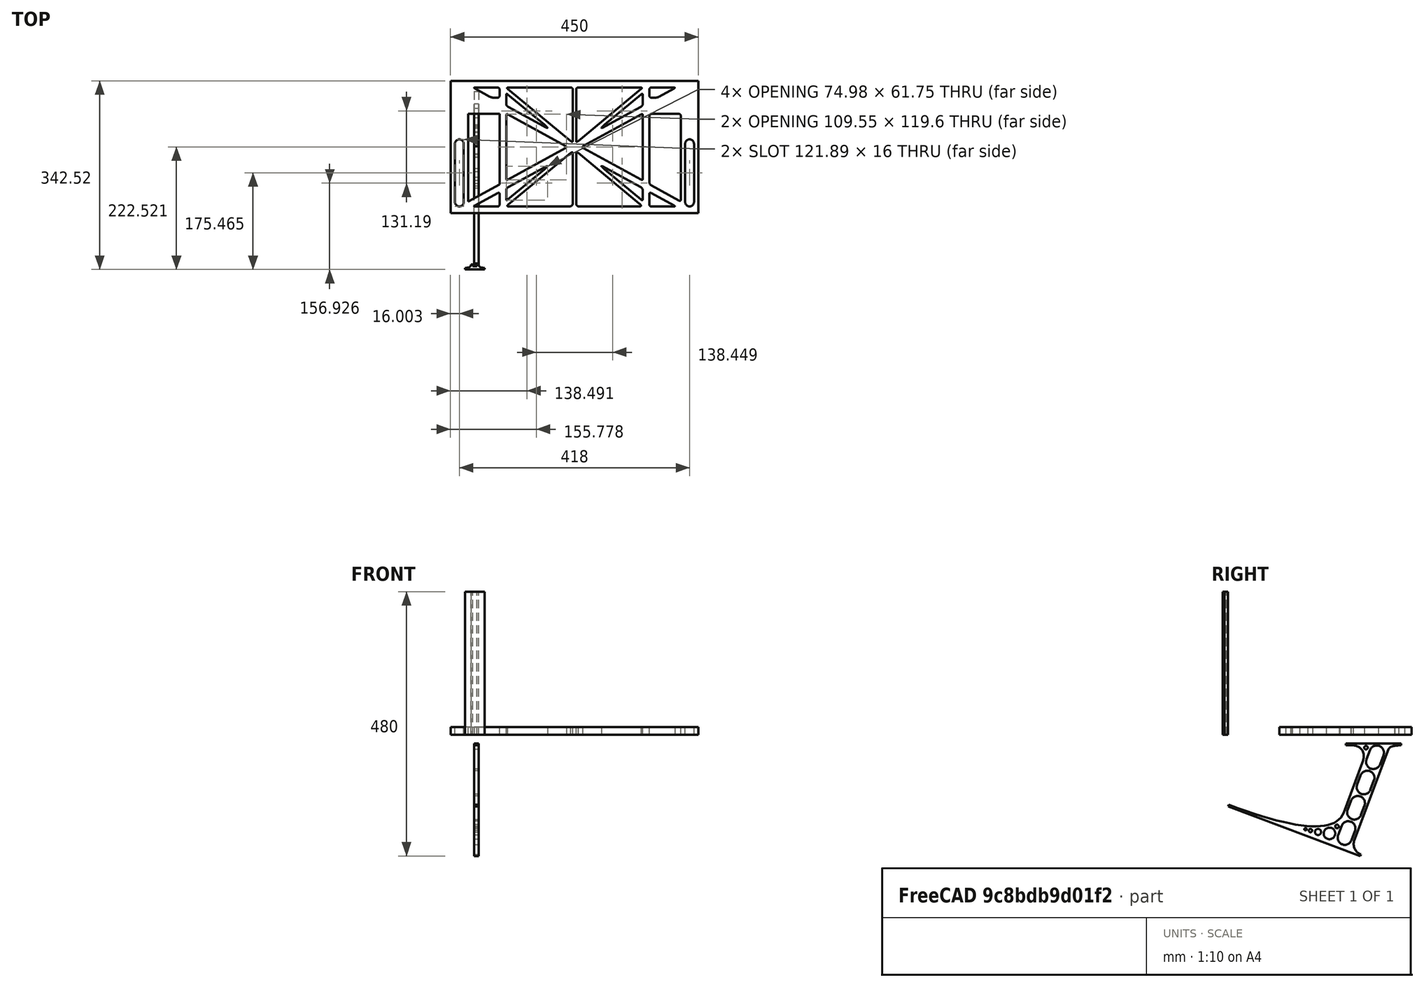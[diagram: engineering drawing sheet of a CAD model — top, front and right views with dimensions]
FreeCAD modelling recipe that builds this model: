
FCSTD DOCUMENT  (FreeCAD 0.19R0.19.2)
Label: laptopStand141FCStd
License: All rights reserved
LicenseURL: http://en.wikipedia.org/wiki/All_rights_reserved
objects: Sketcher::SketchObject×4, Part::Extrusion×3
note: 7 computed .brp shape members not serialized (recipe doc carries the construction recipe); baked Part::Feature solids carry a one-line shape summary decoded from their .brp

FEATURE [Sketcher::SketchObject] Sketch
  FullyConstrained = false
  sketch-geometry (349):
    g0: LineSegment StartX=-10.9272 StartY=-82.7794 StartZ=0 EndX=46.0728 EndY=-51.4823 EndZ=0
    g1: LineSegment StartX=-10.9272 StartY=76.4095 StartZ=0 EndX=-10.9272 EndY=-82.7794 EndZ=0
    g2: LineSegment StartX=46.0728 StartY=76.4095 StartZ=0 EndX=46.0728 EndY=-51.4823 EndZ=0
    g3: LineSegment StartX=-42.9272 StartY=136.221 StartZ=0 EndX=-42.9272 EndY=-103.779 EndZ=0
    g4: LineSegment StartX=407.073 StartY=136.221 StartZ=0 EndX=407.073 EndY=-103.779 EndZ=0
    g5: ArcOfCircle CenterX=-26.9272 CenterY=-83.7794 CenterZ=0 NormalX=0 NormalY=0 NormalZ=1 AngleXU=0 Radius=8 StartAngle=3.14159 EndAngle=6.28319
    g6: ArcOfCircle CenterX=391.073 CenterY=22.1087 CenterZ=0 NormalX=0 NormalY=0 NormalZ=1 AngleXU=0 Radius=8 StartAngle=-4.4e-15 EndAngle=3.14159
    g7: LineSegment StartX=399.073 StartY=22.1087 StartZ=0 EndX=399.073 EndY=-83.7794 EndZ=0
    g8: LineSegment StartX=383.073 StartY=22.1087 StartZ=0 EndX=383.073 EndY=-83.7794 EndZ=0
    g9: ArcOfCircle CenterX=391.073 CenterY=-83.7794 CenterZ=0 NormalX=0 NormalY=0 NormalZ=1 AngleXU=0 Radius=8 StartAngle=3.14159 EndAngle=6.28319
    g10: Circle CenterX=175.022 CenterY=27.0628 CenterZ=0 NormalX=0 NormalY=0 NormalZ=1 AngleXU=0 Radius=1
    g11: Circle CenterX=179.022 CenterY=24.8665 CenterZ=0 NormalX=0 NormalY=0 NormalZ=1 AngleXU=0 Radius=1
    g12: Circle CenterX=179.022 CenterY=27.0628 CenterZ=0 NormalX=0 NormalY=0 NormalZ=1 AngleXU=0 Radius=1
    g13: BSplineCurve PolesCount=3 KnotsCount=2 Degree=2 IsPeriodic=0
    g14: GeomPoint X=175.022 Y=27.0628 Z=0
    g15: GeomPoint X=179.022 Y=27.0628 Z=0
    g16: Circle CenterX=189.124 CenterY=27.0628 CenterZ=0 NormalX=0 NormalY=0 NormalZ=1 AngleXU=0 Radius=1
    g17: Circle CenterX=185.124 CenterY=24.8665 CenterZ=0 NormalX=0 NormalY=0 NormalZ=1 AngleXU=0 Radius=1
    g18: Circle CenterX=185.124 CenterY=27.0628 CenterZ=0 NormalX=0 NormalY=0 NormalZ=1 AngleXU=0 Radius=1
    g19: BSplineCurve PolesCount=3 KnotsCount=2 Degree=2 IsPeriodic=0
    g20: GeomPoint X=189.124 Y=27.0628 Z=0
    g21: GeomPoint X=185.124 Y=27.0628 Z=0
    g22: Circle CenterX=175.022 CenterY=5.37834 CenterZ=0 NormalX=0 NormalY=0 NormalZ=1 AngleXU=0 Radius=1
    g23: Circle CenterX=179.022 CenterY=7.57463 CenterZ=0 NormalX=0 NormalY=0 NormalZ=1 AngleXU=0 Radius=1
    g24: Circle CenterX=179.022 CenterY=5.34704 CenterZ=0 NormalX=0 NormalY=0 NormalZ=1 AngleXU=0 Radius=1
    g25: BSplineCurve PolesCount=3 KnotsCount=2 Degree=2 IsPeriodic=0
    g26: GeomPoint X=175.022 Y=5.37834 Z=0
    g27: GeomPoint X=179.022 Y=5.34704 Z=0
    g28: Circle CenterX=189.124 CenterY=5.37834 CenterZ=0 NormalX=0 NormalY=0 NormalZ=1 AngleXU=0 Radius=1
    g29: Circle CenterX=185.124 CenterY=7.57463 CenterZ=0 NormalX=0 NormalY=0 NormalZ=1 AngleXU=0 Radius=1
    g30: Circle CenterX=185.124 CenterY=5.34704 CenterZ=0 NormalX=0 NormalY=0 NormalZ=1 AngleXU=0 Radius=1
    g31: BSplineCurve PolesCount=3 KnotsCount=2 Degree=2 IsPeriodic=0
    g32: GeomPoint X=189.124 Y=5.37834 Z=0
    g33: GeomPoint X=185.124 Y=5.34704 Z=0
    g34: Circle CenterX=165.871 CenterY=18.1458 CenterZ=0 NormalX=0 NormalY=0 NormalZ=1 AngleXU=0 Radius=1
    g35: Circle CenterX=169.377 CenterY=16.2206 CenterZ=0 NormalX=0 NormalY=0 NormalZ=1 AngleXU=0 Radius=1
    g36: Circle CenterX=165.871 CenterY=14.2954 CenterZ=0 NormalX=0 NormalY=0 NormalZ=1 AngleXU=0 Radius=1
    g37: BSplineCurve PolesCount=3 KnotsCount=2 Degree=2 IsPeriodic=0
    g38: GeomPoint X=165.871 Y=18.1458 Z=0
    g39: GeomPoint X=165.871 Y=14.2954 Z=0
    g40: Circle CenterX=198.275 CenterY=18.1458 CenterZ=0 NormalX=0 NormalY=0 NormalZ=1 AngleXU=0 Radius=1
    g41: Circle CenterX=194.768 CenterY=16.2206 CenterZ=0 NormalX=0 NormalY=0 NormalZ=1 AngleXU=0 Radius=1
    g42: Circle CenterX=198.275 CenterY=14.2954 CenterZ=0 NormalX=0 NormalY=0 NormalZ=1 AngleXU=0 Radius=1
    g43: BSplineCurve PolesCount=3 KnotsCount=2 Degree=2 IsPeriodic=0
    g44: GeomPoint X=198.275 Y=18.1458 Z=0
    g45: GeomPoint X=198.275 Y=14.2954 Z=0
    g46: LineSegment StartX=407.073 StartY=-103.779 StartZ=0 EndX=-42.9272 EndY=-103.779 EndZ=0
    g47: LineSegment StartX=407.073 StartY=136.221 StartZ=0 EndX=-42.9272 EndY=136.221 EndZ=0
    g48: LineSegment StartX=46.0728 StartY=76.4095 StartZ=0 EndX=-10.9272 EndY=76.4095 EndZ=0
    g49: Circle CenterX=125.607 CenterY=54.1951 CenterZ=0 NormalX=0 NormalY=0 NormalZ=1 AngleXU=0 Radius=1
    g50: Circle CenterX=139.632 CenterY=46.4944 CenterZ=0 NormalX=0 NormalY=0 NormalZ=1 AngleXU=0 Radius=1
    g51: Circle CenterX=127.326 CenterY=56.7187 CenterZ=0 NormalX=0 NormalY=0 NormalZ=1 AngleXU=0 Radius=1
    g52: BSplineCurve PolesCount=3 KnotsCount=2 Degree=2 IsPeriodic=0
    g53: GeomPoint X=125.607 Y=54.1951 Z=0
    g54: GeomPoint X=127.326 Y=56.7187 Z=0
    g55: Circle CenterX=236.821 CenterY=56.7187 CenterZ=0 NormalX=0 NormalY=0 NormalZ=1 AngleXU=0 Radius=1
    g56: Circle CenterX=224.513 CenterY=46.4944 CenterZ=0 NormalX=0 NormalY=0 NormalZ=1 AngleXU=0 Radius=1
    g57: Circle CenterX=238.538 CenterY=54.1951 CenterZ=0 NormalX=0 NormalY=0 NormalZ=1 AngleXU=0 Radius=1
    g58: BSplineCurve PolesCount=3 KnotsCount=2 Degree=2 IsPeriodic=0
    g59: GeomPoint X=236.821 Y=56.7187 Z=0
    g60: GeomPoint X=238.538 Y=54.1951 Z=0
    g61: Circle CenterX=238.538 CenterY=-21.7539 CenterZ=0 NormalX=0 NormalY=0 NormalZ=1 AngleXU=0 Radius=1
    g62: Circle CenterX=224.513 CenterY=-14.0532 CenterZ=0 NormalX=0 NormalY=0 NormalZ=1 AngleXU=0 Radius=1
    g63: Circle CenterX=236.821 CenterY=-24.2775 CenterZ=0 NormalX=0 NormalY=0 NormalZ=1 AngleXU=0 Radius=1
    g64: BSplineCurve PolesCount=3 KnotsCount=2 Degree=2 IsPeriodic=0
    g65: GeomPoint X=238.538 Y=-21.7539 Z=0
    g66: GeomPoint X=236.821 Y=-24.2775 Z=0
    g67: Circle CenterX=125.607 CenterY=-21.7539 CenterZ=0 NormalX=0 NormalY=0 NormalZ=1 AngleXU=0 Radius=1
    g68: Circle CenterX=139.632 CenterY=-14.0532 CenterZ=0 NormalX=0 NormalY=0 NormalZ=1 AngleXU=0 Radius=1
    g69: Circle CenterX=127.325 CenterY=-24.2775 CenterZ=0 NormalX=0 NormalY=0 NormalZ=1 AngleXU=0 Radius=1
    g70: BSplineCurve PolesCount=3 KnotsCount=2 Degree=2 IsPeriodic=0
    g71: GeomPoint X=125.607 Y=-21.7539 Z=0
    g72: GeomPoint X=127.325 Y=-24.2775 Z=0
    g73: Circle CenterX=302.996 CenterY=111.695 CenterZ=0 NormalX=0 NormalY=0 NormalZ=1 AngleXU=0 Radius=1
    g74: Circle CenterX=306.073 CenterY=114.251 CenterZ=0 NormalX=0 NormalY=0 NormalZ=1 AngleXU=0 Radius=1
    g75: Circle CenterX=306.073 CenterY=110.251 CenterZ=0 NormalX=0 NormalY=0 NormalZ=1 AngleXU=0 Radius=1
    g76: BSplineCurve PolesCount=3 KnotsCount=2 Degree=2 IsPeriodic=0
    g77: GeomPoint X=302.996 Y=111.695 Z=0
    g78: GeomPoint X=306.073 Y=110.251 Z=0
    g79: Circle CenterX=306.073 CenterY=95.2763 CenterZ=0 NormalX=0 NormalY=0 NormalZ=1 AngleXU=0 Radius=1
    g80: Circle CenterX=306.073 CenterY=91.2763 CenterZ=0 NormalX=0 NormalY=0 NormalZ=1 AngleXU=0 Radius=1
    g81: Circle CenterX=302.567 CenterY=89.3511 CenterZ=0 NormalX=0 NormalY=0 NormalZ=1 AngleXU=0 Radius=1
    g82: BSplineCurve PolesCount=3 KnotsCount=2 Degree=2 IsPeriodic=0
    g83: GeomPoint X=306.073 Y=95.2763 Z=0
    g84: GeomPoint X=302.567 Y=89.3511 Z=0
    g85: LineSegment StartX=306.073 StartY=110.251 StartZ=0 EndX=306.073 EndY=95.2763 EndZ=0
    g86: LineSegment StartX=302.996 StartY=111.695 StartZ=0 EndX=236.821 EndY=56.7187 EndZ=0
    g87: LineSegment StartX=238.538 StartY=54.1951 StartZ=0 EndX=302.567 EndY=89.3511 EndZ=0
    g88: Circle CenterX=61.1496 CenterY=111.695 CenterZ=0 NormalX=0 NormalY=0 NormalZ=1 AngleXU=0 Radius=1
    g89: Circle CenterX=58.0728 CenterY=114.251 CenterZ=0 NormalX=0 NormalY=0 NormalZ=1 AngleXU=0 Radius=1
    g90: Circle CenterX=58.0728 CenterY=110.251 CenterZ=0 NormalX=0 NormalY=0 NormalZ=1 AngleXU=0 Radius=1
    g91: BSplineCurve PolesCount=3 KnotsCount=2 Degree=2 IsPeriodic=0
    g92: GeomPoint X=61.1496 Y=111.695 Z=0
    g93: GeomPoint X=58.0728 Y=110.251 Z=0
    g94: Circle CenterX=61.5791 CenterY=89.3511 CenterZ=0 NormalX=0 NormalY=0 NormalZ=1 AngleXU=0 Radius=1
    g95: Circle CenterX=58.0728 CenterY=91.2763 CenterZ=0 NormalX=0 NormalY=0 NormalZ=1 AngleXU=0 Radius=1
    g96: Circle CenterX=58.0728 CenterY=95.2763 CenterZ=0 NormalX=0 NormalY=0 NormalZ=1 AngleXU=0 Radius=1
    g97: BSplineCurve PolesCount=3 KnotsCount=2 Degree=2 IsPeriodic=0
    g98: GeomPoint X=61.5791 Y=89.3511 Z=0
    g99: GeomPoint X=58.0728 Y=95.2763 Z=0
    g100: LineSegment StartX=58.0728 StartY=110.251 StartZ=0 EndX=58.0728 EndY=95.2763 EndZ=0
    g101: LineSegment StartX=61.1496 StartY=111.695 StartZ=0 EndX=127.326 EndY=56.7187 EndZ=0
    g102: LineSegment StartX=125.607 StartY=54.1951 StartZ=0 EndX=61.5791 EndY=89.3511 EndZ=0
    g103: Circle CenterX=61.5791 CenterY=-56.9099 CenterZ=0 NormalX=0 NormalY=0 NormalZ=1 AngleXU=0 Radius=1
    g104: Circle CenterX=58.0728 CenterY=-58.8351 CenterZ=0 NormalX=0 NormalY=0 NormalZ=1 AngleXU=0 Radius=1
    g105: Circle CenterX=58.0728 CenterY=-62.8351 CenterZ=0 NormalX=0 NormalY=0 NormalZ=1 AngleXU=0 Radius=1
    g106: BSplineCurve PolesCount=3 KnotsCount=2 Degree=2 IsPeriodic=0
    g107: GeomPoint X=61.5791 Y=-56.9099 Z=0
    g108: GeomPoint X=58.0728 Y=-62.8351 Z=0
    g109: Circle CenterX=58.0728 CenterY=-77.8102 CenterZ=0 NormalX=0 NormalY=0 NormalZ=1 AngleXU=0 Radius=1
    g110: Circle CenterX=58.0728 CenterY=-81.8102 CenterZ=0 NormalX=0 NormalY=0 NormalZ=1 AngleXU=0 Radius=1
    g111: Circle CenterX=61.1496 CenterY=-79.2541 CenterZ=0 NormalX=0 NormalY=0 NormalZ=1 AngleXU=0 Radius=1
    g112: BSplineCurve PolesCount=3 KnotsCount=2 Degree=2 IsPeriodic=0
    g113: GeomPoint X=58.0728 Y=-77.8102 Z=0
    g114: GeomPoint X=61.1496 Y=-79.2541 Z=0
    g115: LineSegment StartX=58.0728 StartY=-62.8351 StartZ=0 EndX=58.0728 EndY=-77.8102 EndZ=0
    g116: LineSegment StartX=61.1496 StartY=-79.2541 StartZ=0 EndX=127.325 EndY=-24.2775 EndZ=0
    g117: LineSegment StartX=125.607 StartY=-21.7539 StartZ=0 EndX=61.5791 EndY=-56.9099 EndZ=0
    g118: Circle CenterX=302.567 CenterY=-56.9099 CenterZ=0 NormalX=0 NormalY=0 NormalZ=1 AngleXU=0 Radius=1
    g119: Circle CenterX=306.073 CenterY=-58.8351 CenterZ=0 NormalX=0 NormalY=0 NormalZ=1 AngleXU=0 Radius=1
    g120: Circle CenterX=306.073 CenterY=-62.8351 CenterZ=0 NormalX=0 NormalY=0 NormalZ=1 AngleXU=0 Radius=1
    g121: BSplineCurve PolesCount=3 KnotsCount=2 Degree=2 IsPeriodic=0
    g122: GeomPoint X=302.567 Y=-56.9099 Z=0
    g123: GeomPoint X=306.073 Y=-62.8351 Z=0
    g124: Circle CenterX=302.996 CenterY=-79.2541 CenterZ=0 NormalX=0 NormalY=0 NormalZ=1 AngleXU=0 Radius=1
    g125: Circle CenterX=306.073 CenterY=-81.8102 CenterZ=0 NormalX=0 NormalY=0 NormalZ=1 AngleXU=0 Radius=1
    g126: Circle CenterX=306.073 CenterY=-77.8102 CenterZ=0 NormalX=0 NormalY=0 NormalZ=1 AngleXU=0 Radius=1
    g127: BSplineCurve PolesCount=3 KnotsCount=2 Degree=2 IsPeriodic=0
    g128: GeomPoint X=302.996 Y=-79.2541 Z=0
    g129: GeomPoint X=306.073 Y=-77.8102 Z=0
    g130: LineSegment StartX=306.073 StartY=-62.8351 StartZ=0 EndX=306.073 EndY=-77.8102 EndZ=0
    g131: LineSegment StartX=302.996 StartY=-79.2541 StartZ=0 EndX=236.821 EndY=-24.2775 EndZ=0
    g132: LineSegment StartX=238.538 StartY=-21.7539 StartZ=0 EndX=302.567 EndY=-56.9099 EndZ=0
    g133: Circle CenterX=61.6457 CenterY=-88.8112 CenterZ=0 NormalX=0 NormalY=0 NormalZ=1 AngleXU=0 Radius=1
    g134: Circle CenterX=58.0728 CenterY=-91.7794 CenterZ=0 NormalX=0 NormalY=0 NormalZ=1 AngleXU=0 Radius=1
    g135: Circle CenterX=63.9135 CenterY=-91.7794 CenterZ=0 NormalX=0 NormalY=0 NormalZ=1 AngleXU=0 Radius=1
    g136: BSplineCurve PolesCount=3 KnotsCount=2 Degree=2 IsPeriodic=0
    g137: GeomPoint X=61.6457 Y=-88.8112 Z=0
    g138: GeomPoint X=63.9135 Y=-91.7794 Z=0
    g139: Circle CenterX=179.022 CenterY=-85.8163 CenterZ=0 NormalX=0 NormalY=0 NormalZ=1 AngleXU=0 Radius=1
    g140: Circle CenterX=179.022 CenterY=-91.7794 CenterZ=0 NormalX=0 NormalY=0 NormalZ=1 AngleXU=0 Radius=1
    g141: Circle CenterX=171.895 CenterY=-91.7794 CenterZ=0 NormalX=0 NormalY=0 NormalZ=1 AngleXU=0 Radius=1
    g142: BSplineCurve PolesCount=3 KnotsCount=2 Degree=2 IsPeriodic=0
    g143: GeomPoint X=179.022 Y=-85.8163 Z=0
    g144: GeomPoint X=171.895 Y=-91.7794 Z=0
    g145: Circle CenterX=185.124 CenterY=-86.2028 CenterZ=0 NormalX=0 NormalY=0 NormalZ=1 AngleXU=0 Radius=1
    g146: Circle CenterX=185.124 CenterY=-91.7794 CenterZ=0 NormalX=0 NormalY=0 NormalZ=1 AngleXU=0 Radius=1
    g147: Circle CenterX=191.747 CenterY=-91.7794 CenterZ=0 NormalX=0 NormalY=0 NormalZ=1 AngleXU=0 Radius=1
    g148: BSplineCurve PolesCount=3 KnotsCount=2 Degree=2 IsPeriodic=0
    g149: GeomPoint X=185.124 Y=-86.2028 Z=0
    g150: GeomPoint X=191.747 Y=-91.7794 Z=0
    g151: Circle CenterX=299.888 CenterY=-86.6413 CenterZ=0 NormalX=0 NormalY=0 NormalZ=1 AngleXU=0 Radius=1
    g152: Circle CenterX=306.073 CenterY=-91.7794 CenterZ=0 NormalX=0 NormalY=0 NormalZ=1 AngleXU=0 Radius=1
    g153: Circle CenterX=298.776 CenterY=-91.7794 CenterZ=0 NormalX=0 NormalY=0 NormalZ=1 AngleXU=0 Radius=1
    g154: BSplineCurve PolesCount=3 KnotsCount=2 Degree=2 IsPeriodic=0
    g155: GeomPoint X=299.888 Y=-86.6413 Z=0
    g156: GeomPoint X=298.776 Y=-91.7794 Z=0
    g157: LineSegment StartX=189.124 StartY=5.37834 StartZ=0 EndX=299.888 EndY=-86.6413 EndZ=0
    g158: LineSegment StartX=298.776 StartY=-91.7794 StartZ=0 EndX=191.747 EndY=-91.7794 EndZ=0
    g159: LineSegment StartX=185.124 StartY=-86.2028 StartZ=0 EndX=185.124 EndY=5.34704 EndZ=0
    g160: LineSegment StartX=179.022 StartY=5.34704 StartZ=0 EndX=179.022 EndY=-85.8163 EndZ=0
    g161: LineSegment StartX=171.895 StartY=-91.7794 StartZ=0 EndX=63.9135 EndY=-91.7794 EndZ=0
    g162: LineSegment StartX=61.6457 StartY=-88.8112 StartZ=0 EndX=175.022 EndY=5.37834 EndZ=0
    g163: Circle CenterX=302.073 CenterY=124.221 CenterZ=0 NormalX=0 NormalY=0 NormalZ=1 AngleXU=0 Radius=1
    g164: Circle CenterX=306.073 CenterY=124.221 CenterZ=0 NormalX=0 NormalY=0 NormalZ=1 AngleXU=0 Radius=1
    g165: Circle CenterX=302.996 CenterY=121.665 CenterZ=0 NormalX=0 NormalY=0 NormalZ=1 AngleXU=0 Radius=1
    g166: BSplineCurve PolesCount=3 KnotsCount=2 Degree=2 IsPeriodic=0
    g167: GeomPoint X=302.073 Y=124.221 Z=0
    g168: GeomPoint X=302.996 Y=121.665 Z=0
    g169: Circle CenterX=189.124 CenterY=124.221 CenterZ=0 NormalX=0 NormalY=0 NormalZ=1 AngleXU=0 Radius=1
    g170: Circle CenterX=185.124 CenterY=124.221 CenterZ=0 NormalX=0 NormalY=0 NormalZ=1 AngleXU=0 Radius=1
    g171: Circle CenterX=185.124 CenterY=120.221 CenterZ=0 NormalX=0 NormalY=0 NormalZ=1 AngleXU=0 Radius=1
    g172: BSplineCurve PolesCount=3 KnotsCount=2 Degree=2 IsPeriodic=0
    g173: GeomPoint X=189.124 Y=124.221 Z=0
    g174: GeomPoint X=185.124 Y=120.221 Z=0
    g175: Circle CenterX=175.022 CenterY=124.221 CenterZ=0 NormalX=0 NormalY=0 NormalZ=1 AngleXU=0 Radius=1
    g176: Circle CenterX=179.022 CenterY=124.221 CenterZ=0 NormalX=0 NormalY=0 NormalZ=1 AngleXU=0 Radius=1
    g177: Circle CenterX=179.022 CenterY=120.221 CenterZ=0 NormalX=0 NormalY=0 NormalZ=1 AngleXU=0 Radius=1
    g178: BSplineCurve PolesCount=3 KnotsCount=2 Degree=2 IsPeriodic=0
    g179: GeomPoint X=175.022 Y=124.221 Z=0
    g180: GeomPoint X=179.022 Y=120.221 Z=0
    g181: Circle CenterX=62.0728 CenterY=124.221 CenterZ=0 NormalX=0 NormalY=0 NormalZ=1 AngleXU=0 Radius=1
    g182: Circle CenterX=58.0728 CenterY=124.221 CenterZ=0 NormalX=0 NormalY=0 NormalZ=1 AngleXU=0 Radius=1
    g183: Circle CenterX=61.1496 CenterY=121.665 CenterZ=0 NormalX=0 NormalY=0 NormalZ=1 AngleXU=0 Radius=1
    g184: BSplineCurve PolesCount=3 KnotsCount=2 Degree=2 IsPeriodic=0
    g185: GeomPoint X=62.0728 Y=124.221 Z=0
    g186: GeomPoint X=61.1496 Y=121.665 Z=0
    g187: LineSegment StartX=62.0728 StartY=124.221 StartZ=0 EndX=175.022 EndY=124.221 EndZ=0
    g188: LineSegment StartX=179.022 StartY=120.221 StartZ=0 EndX=179.022 EndY=27.0628 EndZ=0
    g189: LineSegment StartX=185.124 StartY=27.0628 StartZ=0 EndX=185.124 EndY=120.221 EndZ=0
    g190: LineSegment StartX=189.124 StartY=124.221 StartZ=0 EndX=302.073 EndY=124.221 EndZ=0
    g191: LineSegment StartX=302.996 StartY=121.665 StartZ=0 EndX=189.124 EndY=27.0628 EndZ=0
    g192: LineSegment StartX=175.022 StartY=27.0628 StartZ=0 EndX=61.1496 EndY=121.665 EndZ=0
    g193: Circle CenterX=61.5791 CenterY=75.4095 CenterZ=0 NormalX=0 NormalY=0 NormalZ=1 AngleXU=0 Radius=1
    g194: Circle CenterX=58.0728 CenterY=77.3346 CenterZ=0 NormalX=0 NormalY=0 NormalZ=1 AngleXU=0 Radius=1
    g195: Circle CenterX=58.0728 CenterY=73.3346 CenterZ=0 NormalX=0 NormalY=0 NormalZ=1 AngleXU=0 Radius=1
    g196: BSplineCurve PolesCount=3 KnotsCount=2 Degree=2 IsPeriodic=0
    g197: GeomPoint X=61.5791 Y=75.4095 Z=0
    g198: GeomPoint X=58.0728 Y=73.3346 Z=0
    g199: Circle CenterX=58.0728 CenterY=-40.8935 CenterZ=0 NormalX=0 NormalY=0 NormalZ=1 AngleXU=0 Radius=1
    g200: Circle CenterX=58.0728 CenterY=-44.8935 CenterZ=0 NormalX=0 NormalY=0 NormalZ=1 AngleXU=0 Radius=1
    g201: Circle CenterX=61.5791 CenterY=-42.9683 CenterZ=0 NormalX=0 NormalY=0 NormalZ=1 AngleXU=0 Radius=1
    g202: BSplineCurve PolesCount=3 KnotsCount=2 Degree=2 IsPeriodic=0
    g203: GeomPoint X=58.0728 Y=-40.8935 Z=0
    g204: GeomPoint X=61.5791 Y=-42.9683 Z=0
    g205: LineSegment StartX=61.5791 StartY=-42.9683 StartZ=0 EndX=165.871 EndY=14.2954 EndZ=0
    g206: LineSegment StartX=165.871 StartY=18.1458 StartZ=0 EndX=61.5791 EndY=75.4095 EndZ=0
    g207: LineSegment StartX=58.0728 StartY=73.3346 StartZ=0 EndX=58.0728 EndY=-40.8935 EndZ=0
    g208: Circle CenterX=302.567 CenterY=-42.9683 CenterZ=0 NormalX=0 NormalY=0 NormalZ=1 AngleXU=0 Radius=1
    g209: Circle CenterX=306.073 CenterY=-44.8935 CenterZ=0 NormalX=0 NormalY=0 NormalZ=1 AngleXU=0 Radius=1
    g210: Circle CenterX=306.073 CenterY=-40.8935 CenterZ=0 NormalX=0 NormalY=0 NormalZ=1 AngleXU=0 Radius=1
    g211: BSplineCurve PolesCount=3 KnotsCount=2 Degree=2 IsPeriodic=0
    g212: GeomPoint X=302.567 Y=-42.9683 Z=0
    g213: GeomPoint X=306.073 Y=-40.8935 Z=0
    g214: Circle CenterX=306.073 CenterY=73.3346 CenterZ=0 NormalX=0 NormalY=0 NormalZ=1 AngleXU=0 Radius=1
    g215: Circle CenterX=306.073 CenterY=77.3346 CenterZ=0 NormalX=0 NormalY=0 NormalZ=1 AngleXU=0 Radius=1
    g216: Circle CenterX=302.567 CenterY=75.4095 CenterZ=0 NormalX=0 NormalY=0 NormalZ=1 AngleXU=0 Radius=1
    g217: BSplineCurve PolesCount=3 KnotsCount=2 Degree=2 IsPeriodic=0
    g218: GeomPoint X=306.073 Y=73.3346 Z=0
    g219: GeomPoint X=302.567 Y=75.4095 Z=0
    g220: LineSegment StartX=302.567 StartY=-42.9683 StartZ=0 EndX=198.275 EndY=14.2954 EndZ=0
    g221: LineSegment StartX=198.275 StartY=18.1458 StartZ=0 EndX=302.567 EndY=75.4095 EndZ=0
    g222: LineSegment StartX=306.073 StartY=73.3346 StartZ=0 EndX=306.073 EndY=-40.8935 EndZ=0
    g223: LineSegment StartX=322.073 StartY=105.865 StartZ=0 EndX=328.643 EndY=105.865 EndZ=0
    g224: LineSegment StartX=318.073 StartY=120.221 StartZ=0 EndX=318.073 EndY=109.865 EndZ=0
    g225: LineSegment StartX=336.157 StartY=107.779 StartZ=0 EndX=362.567 EndY=122.294 EndZ=0
    g226: Circle CenterX=362.073 CenterY=124.221 CenterZ=0 NormalX=0 NormalY=0 NormalZ=1 AngleXU=0 Radius=1
    g227: Circle CenterX=366.073 CenterY=124.221 CenterZ=0 NormalX=0 NormalY=0 NormalZ=1 AngleXU=0 Radius=1
    g228: Circle CenterX=362.567 CenterY=122.294 CenterZ=0 NormalX=0 NormalY=0 NormalZ=1 AngleXU=0 Radius=1
    g229: BSplineCurve PolesCount=3 KnotsCount=2 Degree=2 IsPeriodic=0
    g230: GeomPoint X=362.073 Y=124.221 Z=0
    g231: GeomPoint X=362.567 Y=122.294 Z=0
    g232: Circle CenterX=322.073 CenterY=124.221 CenterZ=0 NormalX=0 NormalY=0 NormalZ=1 AngleXU=0 Radius=1
    g233: Circle CenterX=318.073 CenterY=124.221 CenterZ=0 NormalX=0 NormalY=0 NormalZ=1 AngleXU=0 Radius=1
    g234: Circle CenterX=318.073 CenterY=120.221 CenterZ=0 NormalX=0 NormalY=0 NormalZ=1 AngleXU=0 Radius=1
    g235: BSplineCurve PolesCount=3 KnotsCount=2 Degree=2 IsPeriodic=0
    g236: GeomPoint X=322.073 Y=124.221 Z=0
    g237: GeomPoint X=318.073 Y=120.221 Z=0
    g238: Circle CenterX=322.073 CenterY=105.865 CenterZ=0 NormalX=0 NormalY=0 NormalZ=1 AngleXU=0 Radius=1
    g239: Circle CenterX=318.073 CenterY=105.865 CenterZ=0 NormalX=0 NormalY=0 NormalZ=1 AngleXU=0 Radius=1
    g240: Circle CenterX=318.073 CenterY=109.865 CenterZ=0 NormalX=0 NormalY=0 NormalZ=1 AngleXU=0 Radius=1
    g241: BSplineCurve PolesCount=3 KnotsCount=2 Degree=2 IsPeriodic=0
    g242: GeomPoint X=322.073 Y=105.865 Z=0
    g243: GeomPoint X=318.073 Y=109.865 Z=0
    g244: Circle CenterX=336.157 CenterY=107.779 CenterZ=0 NormalX=0 NormalY=0 NormalZ=1 AngleXU=0 Radius=1
    g245: Circle CenterX=332.651 CenterY=105.853 CenterZ=0 NormalX=0 NormalY=0 NormalZ=1 AngleXU=0 Radius=1
    g246: Circle CenterX=328.643 CenterY=105.865 CenterZ=0 NormalX=0 NormalY=0 NormalZ=1 AngleXU=0 Radius=1
    g247: BSplineCurve PolesCount=3 KnotsCount=2 Degree=2 IsPeriodic=0
    g248: GeomPoint X=336.157 Y=107.779 Z=0
    g249: GeomPoint X=328.643 Y=105.865 Z=0
    g250: LineSegment StartX=322.073 StartY=124.221 StartZ=0 EndX=362.073 EndY=124.221 EndZ=0
    g251: Circle CenterX=371.567 CenterY=-80.8644 CenterZ=0 NormalX=0 NormalY=0 NormalZ=1 AngleXU=0 Radius=1
    g252: Circle CenterX=375.073 CenterY=-82.7896 CenterZ=0 NormalX=0 NormalY=0 NormalZ=1 AngleXU=0 Radius=1
    g253: Circle CenterX=375.073 CenterY=-78.7896 CenterZ=0 NormalX=0 NormalY=0 NormalZ=1 AngleXU=0 Radius=1
    g254: BSplineCurve PolesCount=3 KnotsCount=2 Degree=2 IsPeriodic=0
    g255: GeomPoint X=371.567 Y=-80.8644 Z=0
    g256: GeomPoint X=375.073 Y=-78.7896 Z=0
    g257: Circle CenterX=321.579 CenterY=-53.4075 CenterZ=0 NormalX=0 NormalY=0 NormalZ=1 AngleXU=0 Radius=1
    g258: Circle CenterX=318.073 CenterY=-51.4823 CenterZ=0 NormalX=0 NormalY=0 NormalZ=1 AngleXU=0 Radius=1
    g259: Circle CenterX=318.073 CenterY=-47.4805 CenterZ=0 NormalX=0 NormalY=0 NormalZ=1 AngleXU=0 Radius=1
    g260: BSplineCurve PolesCount=3 KnotsCount=2 Degree=2 IsPeriodic=0
    g261: GeomPoint X=321.579 Y=-53.4075 Z=0
    g262: GeomPoint X=318.073 Y=-47.4805 Z=0
    g263: LineSegment StartX=371.567 StartY=-80.8644 StartZ=0 EndX=321.579 EndY=-53.4075 EndZ=0
    g264: Circle CenterX=321.579 CenterY=-67.3492 CenterZ=0 NormalX=0 NormalY=0 NormalZ=1 AngleXU=0 Radius=1
    g265: Circle CenterX=318.073 CenterY=-65.424 CenterZ=0 NormalX=0 NormalY=0 NormalZ=1 AngleXU=0 Radius=1
    g266: Circle CenterX=318.073 CenterY=-69.424 CenterZ=0 NormalX=0 NormalY=0 NormalZ=1 AngleXU=0 Radius=1
    g267: BSplineCurve PolesCount=3 KnotsCount=2 Degree=2 IsPeriodic=0
    g268: GeomPoint X=321.579 Y=-67.3492 Z=0
    g269: GeomPoint X=318.073 Y=-69.424 Z=0
    g270: Circle CenterX=362.567 CenterY=-89.8542 CenterZ=0 NormalX=0 NormalY=0 NormalZ=1 AngleXU=0 Radius=1
    g271: Circle CenterX=366.073 CenterY=-91.7794 CenterZ=0 NormalX=0 NormalY=0 NormalZ=1 AngleXU=0 Radius=1
    g272: Circle CenterX=362.073 CenterY=-91.7794 CenterZ=0 NormalX=0 NormalY=0 NormalZ=1 AngleXU=0 Radius=1
    g273: BSplineCurve PolesCount=3 KnotsCount=2 Degree=2 IsPeriodic=0
    g274: GeomPoint X=362.567 Y=-89.8542 Z=0
    g275: GeomPoint X=362.073 Y=-91.7794 Z=0
    g276: Circle CenterX=322.073 CenterY=-91.7794 CenterZ=0 NormalX=0 NormalY=0 NormalZ=1 AngleXU=0 Radius=1
    g277: Circle CenterX=318.073 CenterY=-91.7794 CenterZ=0 NormalX=0 NormalY=0 NormalZ=1 AngleXU=0 Radius=1
    g278: Circle CenterX=318.073 CenterY=-87.7794 CenterZ=0 NormalX=0 NormalY=0 NormalZ=1 AngleXU=0 Radius=1
    g279: BSplineCurve PolesCount=3 KnotsCount=2 Degree=2 IsPeriodic=0
    g280: GeomPoint X=322.073 Y=-91.7794 Z=0
    g281: GeomPoint X=318.073 Y=-87.7794 Z=0
    g282: LineSegment StartX=362.567 StartY=-89.8542 StartZ=0 EndX=321.579 EndY=-67.3492 EndZ=0
    g283: LineSegment StartX=318.073 StartY=-69.424 StartZ=0 EndX=318.073 EndY=-87.7794 EndZ=0
    g284: LineSegment StartX=322.073 StartY=-91.7794 StartZ=0 EndX=362.073 EndY=-91.7794 EndZ=0
    g285: Circle CenterX=2.07281 CenterY=124.221 CenterZ=0 NormalX=0 NormalY=0 NormalZ=1 AngleXU=0 Radius=1
    g286: Circle CenterX=1.57905 CenterY=122.295 CenterZ=0 NormalX=0 NormalY=0 NormalZ=1 AngleXU=0 Radius=1
    g287: BSplineCurve PolesCount=3 KnotsCount=2 Degree=2 IsPeriodic=0
    g288: GeomPoint X=2.07281 Y=124.221 Z=0
    g289: GeomPoint X=1.57905 Y=122.295 Z=0
    g290: Circle CenterX=42.0728 CenterY=124.221 CenterZ=0 NormalX=0 NormalY=0 NormalZ=1 AngleXU=0 Radius=1
    g291: Circle CenterX=46.0728 CenterY=124.221 CenterZ=0 NormalX=0 NormalY=0 NormalZ=1 AngleXU=0 Radius=1
    g292: Circle CenterX=46.0728 CenterY=120.221 CenterZ=0 NormalX=0 NormalY=0 NormalZ=1 AngleXU=0 Radius=1
    g293: BSplineCurve PolesCount=3 KnotsCount=2 Degree=2 IsPeriodic=0
    g294: GeomPoint X=42.0728 Y=124.221 Z=0
    g295: GeomPoint X=46.0728 Y=120.221 Z=0
    g296: Circle CenterX=46.0728 CenterY=109.865 CenterZ=0 NormalX=0 NormalY=0 NormalZ=1 AngleXU=0 Radius=1
    g297: Circle CenterX=46.0728 CenterY=105.865 CenterZ=0 NormalX=0 NormalY=0 NormalZ=1 AngleXU=0 Radius=1
    g298: Circle CenterX=42.0728 CenterY=105.865 CenterZ=0 NormalX=0 NormalY=0 NormalZ=1 AngleXU=0 Radius=1
    g299: BSplineCurve PolesCount=3 KnotsCount=2 Degree=2 IsPeriodic=0
    g300: GeomPoint X=46.0728 Y=109.865 Z=0
    g301: GeomPoint X=42.0728 Y=105.865 Z=0
    g302: Circle CenterX=35.5028 CenterY=105.865 CenterZ=0 NormalX=0 NormalY=0 NormalZ=1 AngleXU=0 Radius=1
    g303: Circle CenterX=31.5028 CenterY=105.865 CenterZ=0 NormalX=0 NormalY=0 NormalZ=1 AngleXU=0 Radius=1
    g304: Circle CenterX=27.9965 CenterY=107.79 CenterZ=0 NormalX=0 NormalY=0 NormalZ=1 AngleXU=0 Radius=1
    g305: BSplineCurve PolesCount=3 KnotsCount=2 Degree=2 IsPeriodic=0
    g306: GeomPoint X=35.5028 Y=105.865 Z=0
    g307: GeomPoint X=27.9965 Y=107.79 Z=0
    g308: LineSegment StartX=2.07281 StartY=124.221 StartZ=0 EndX=42.0728 EndY=124.221 EndZ=0
    g309: LineSegment StartX=46.0728 StartY=120.221 StartZ=0 EndX=46.0728 EndY=109.865 EndZ=0
    g310: LineSegment StartX=42.0728 StartY=105.865 StartZ=0 EndX=35.5028 EndY=105.865 EndZ=0
    g311: LineSegment StartX=27.9965 StartY=107.79 StartZ=0 EndX=1.57905 EndY=122.295 EndZ=0
    g312: Circle CenterX=42.5666 CenterY=-67.3492 CenterZ=0 NormalX=0 NormalY=0 NormalZ=1 AngleXU=0 Radius=1
    g313: Circle CenterX=46.0728 CenterY=-65.424 CenterZ=0 NormalX=0 NormalY=0 NormalZ=1 AngleXU=0 Radius=1
    g314: Circle CenterX=46.0728 CenterY=-69.424 CenterZ=0 NormalX=0 NormalY=0 NormalZ=1 AngleXU=0 Radius=1
    g315: BSplineCurve PolesCount=3 KnotsCount=2 Degree=2 IsPeriodic=0
    g316: GeomPoint X=42.5666 Y=-67.3492 Z=0
    g317: GeomPoint X=46.0728 Y=-69.424 Z=0
    g318: Circle CenterX=46.0728 CenterY=-87.7794 CenterZ=0 NormalX=0 NormalY=0 NormalZ=1 AngleXU=0 Radius=1
    g319: Circle CenterX=46.0728 CenterY=-91.7794 CenterZ=0 NormalX=0 NormalY=0 NormalZ=1 AngleXU=0 Radius=1
    g320: Circle CenterX=42.0728 CenterY=-91.7794 CenterZ=0 NormalX=0 NormalY=0 NormalZ=1 AngleXU=0 Radius=1
    g321: BSplineCurve PolesCount=3 KnotsCount=2 Degree=2 IsPeriodic=0
    g322: GeomPoint X=46.0728 Y=-87.7794 Z=0
    g323: GeomPoint X=42.0728 Y=-91.7794 Z=0
    g324: Circle CenterX=2.07281 CenterY=-91.7794 CenterZ=0 NormalX=0 NormalY=0 NormalZ=1 AngleXU=0 Radius=1
    g325: Circle CenterX=-1.92719 CenterY=-91.7794 CenterZ=0 NormalX=0 NormalY=0 NormalZ=1 AngleXU=0 Radius=1
    g326: Circle CenterX=1.57905 CenterY=-89.8542 CenterZ=0 NormalX=0 NormalY=0 NormalZ=1 AngleXU=0 Radius=1
    g327: BSplineCurve PolesCount=3 KnotsCount=2 Degree=2 IsPeriodic=0
    g328: GeomPoint X=2.07281 Y=-91.7794 Z=0
    g329: GeomPoint X=1.57905 Y=-89.8542 Z=0
    g330: LineSegment StartX=2.07281 StartY=-91.7794 StartZ=0 EndX=42.0728 EndY=-91.7794 EndZ=0
    g331: LineSegment StartX=46.0728 StartY=-87.7794 StartZ=0 EndX=46.0728 EndY=-69.424 EndZ=0
    g332: LineSegment StartX=42.5666 StartY=-67.3492 StartZ=0 EndX=1.57905 EndY=-89.8542 EndZ=0
    g333: Circle CenterX=322.073 CenterY=76.4095 CenterZ=0 NormalX=0 NormalY=0 NormalZ=1 AngleXU=0 Radius=4
    g334: BSplineCurve PolesCount=3 KnotsCount=2 Degree=2 IsPeriodic=0
    g335: GeomPoint X=318.073 Y=72.4095 Z=0
    g336: GeomPoint X=322.073 Y=76.4095 Z=0
    g337: Circle CenterX=375.073 CenterY=72.4095 CenterZ=0 NormalX=0 NormalY=0 NormalZ=1 AngleXU=0 Radius=1
    g338: Circle CenterX=375.073 CenterY=76.4095 CenterZ=0 NormalX=0 NormalY=0 NormalZ=1 AngleXU=0 Radius=1
    g339: Circle CenterX=371.073 CenterY=76.4095 CenterZ=0 NormalX=0 NormalY=0 NormalZ=1 AngleXU=0 Radius=1
    g340: BSplineCurve PolesCount=3 KnotsCount=2 Degree=2 IsPeriodic=0
    g341: GeomPoint X=375.073 Y=72.4095 Z=0
    g342: GeomPoint X=371.073 Y=76.4095 Z=0
    g343: LineSegment StartX=322.073 StartY=76.4095 StartZ=0 EndX=371.073 EndY=76.4095 EndZ=0
    g344: LineSegment StartX=318.073 StartY=72.4095 StartZ=0 EndX=318.073 EndY=-47.4805 EndZ=0
    g345: LineSegment StartX=375.073 StartY=72.4095 StartZ=0 EndX=375.073 EndY=-78.7896 EndZ=0
    g346: ArcOfCircle CenterX=-26.9272 CenterY=22.1087 CenterZ=0 NormalX=0 NormalY=0 NormalZ=1 AngleXU=0 Radius=4 StartAngle=5e-16 EndAngle=3.14159
    g347: LineSegment StartX=-30.9272 StartY=22.1087 StartZ=0 EndX=-34.9272 EndY=-83.7794 EndZ=0
    g348: LineSegment StartX=-18.9272 StartY=-83.7794 StartZ=0 EndX=-22.9272 EndY=22.1087 EndZ=0
  constraints (572):
    c: Coincident(g0,g2)
    c: Block(g0)
    c: Block(g1)
    c: Vertical(g3)
    c: Vertical(g4)
    c: Block(g4)
    c: Block(g3)
    c: Tangent(g6,g7) = 1.5708
    c: Tangent(g7,g9) = 1.5708
    c: Equal(g6,g9)
    c: Coincident(g8,g6)
    c: Coincident(g8,g9)
    c: Block(g7)
    c: Block(g8)
    c: Weight(g10) = 1
    c: Equal(g10,g11)
    c: Equal(g10,g12)
    c: InternalAlignment(g10,g13)
    c: InternalAlignment(g11,g13)
    c: InternalAlignment(g12,g13)
    c: InternalAlignment(g14,g13)
    c: InternalAlignment(g15,g13)
    c: Weight(g16) = 1
    c: Equal(g16,g17)
    c: Equal(g16,g18)
    c: InternalAlignment(g16,g19)
    c: InternalAlignment(g17,g19)
    c: InternalAlignment(g18,g19)
    c: InternalAlignment(g20,g19)
    c: InternalAlignment(g21,g19)
    c: Block(g19)
    c: Block(g13)
    c: Weight(g22) = 1
    c: Equal(g22,g23)
    c: Equal(g22,g24)
    c: InternalAlignment(g22,g25)
    c: InternalAlignment(g23,g25)
    c: InternalAlignment(g24,g25)
    c: InternalAlignment(g26,g25)
    c: InternalAlignment(g27,g25)
    c: Weight(g28) = 1
    c: Equal(g28,g29)
    c: Equal(g28,g30)
    c: InternalAlignment(g28,g31)
    c: InternalAlignment(g29,g31)
    c: InternalAlignment(g30,g31)
    c: InternalAlignment(g32,g31)
    c: InternalAlignment(g33,g31)
    c: Block(g31)
    c: Block(g25)
    c: Weight(g34) = 1
    c: Equal(g34,g35)
    c: Equal(g34,g36)
    c: InternalAlignment(g34,g37)
    c: InternalAlignment(g35,g37)
    c: InternalAlignment(g36,g37)
    c: InternalAlignment(g38,g37)
    c: InternalAlignment(g39,g37)
    c: Weight(g40) = 1
    c: Equal(g40,g41)
    c: Equal(g40,g42)
    c: InternalAlignment(g40,g43)
    c: InternalAlignment(g41,g43)
    c: InternalAlignment(g42,g43)
    c: InternalAlignment(g44,g43)
    c: InternalAlignment(g45,g43)
    c: Block(g37)
    c: Block(g43)
    c: Coincident(g46,g4)
    c: Coincident(g46,g3)
    c: Horizontal(g46)
    c: Distance(g46) = 450
    c: Coincident(g47,g4)
    c: Coincident(g47,g3)
    c: Horizontal(g47)
    c: Horizontal(g48)
    c: Coincident(g2,g48)
    c: Block(g48)
    c: Coincident(g1,g48)
    c: Weight(g49) = 1
    c: Equal(g49,g50)
    c: Equal(g49,g51)
    c: InternalAlignment(g49,g52)
    c: InternalAlignment(g50,g52)
    c: InternalAlignment(g51,g52)
    c: InternalAlignment(g53,g52)
    c: InternalAlignment(g54,g52)
    c: Block(g52)
    c: Weight(g55) = 1
    c: Equal(g55,g56)
    c: Equal(g55,g57)
    c: InternalAlignment(g55,g58)
    c: InternalAlignment(g56,g58)
    c: InternalAlignment(g57,g58)
    c: InternalAlignment(g59,g58)
    c: InternalAlignment(g60,g58)
    c: Block(g58)
    c: Weight(g61) = 1
    c: Equal(g61,g62)
    c: Equal(g61,g63)
    c: InternalAlignment(g61,g64)
    c: InternalAlignment(g62,g64)
    c: InternalAlignment(g63,g64)
    c: InternalAlignment(g65,g64)
    c: InternalAlignment(g66,g64)
    c: Block(g64)
    c: Weight(g67) = 1
    c: Equal(g67,g68)
    c: Equal(g67,g69)
    c: InternalAlignment(g67,g70)
    c: InternalAlignment(g68,g70)
    c: InternalAlignment(g69,g70)
    c: InternalAlignment(g71,g70)
    c: InternalAlignment(g72,g70)
    c: Block(g70)
    c: Weight(g73) = 1
    c: Equal(g73,g74)
    c: Equal(g73,g75)
    c: InternalAlignment(g73,g76)
    c: InternalAlignment(g74,g76)
    c: InternalAlignment(g75,g76)
    c: InternalAlignment(g77,g76)
    c: InternalAlignment(g78,g76)
    c: Weight(g79) = 1
    c: Equal(g79,g80)
    c: Equal(g79,g81)
    c: InternalAlignment(g79,g82)
    c: InternalAlignment(g80,g82)
    c: InternalAlignment(g81,g82)
    c: InternalAlignment(g83,g82)
    c: InternalAlignment(g84,g82)
    c: Block(g76)
    c: Block(g82)
    c: Coincident(g85,g76)
    c: Coincident(g85,g82)
    c: Vertical(g85)
    c: Coincident(g86,g76)
    c: Coincident(g86,g58)
    c: Coincident(g87,g58)
    c: Coincident(g87,g82)
    c: Weight(g88) = 1
    c: Equal(g88,g89)
    c: Equal(g88,g90)
    c: InternalAlignment(g88,g91)
    c: InternalAlignment(g89,g91)
    c: InternalAlignment(g90,g91)
    c: InternalAlignment(g92,g91)
    c: InternalAlignment(g93,g91)
    c: Weight(g94) = 1
    c: Equal(g94,g95)
    c: Equal(g94,g96)
    c: InternalAlignment(g94,g97)
    c: InternalAlignment(g95,g97)
    c: InternalAlignment(g96,g97)
    c: InternalAlignment(g98,g97)
    c: InternalAlignment(g99,g97)
    c: Block(g91)
    c: Block(g97)
    c: Coincident(g100,g91)
    c: Coincident(g100,g97)
    c: Vertical(g100)
    c: Coincident(g101,g91)
    c: Coincident(g101,g52)
    c: Coincident(g102,g52)
    c: Coincident(g102,g97)
    c: Weight(g103) = 1
    c: Equal(g103,g104)
    c: Equal(g103,g105)
    c: InternalAlignment(g103,g106)
    c: InternalAlignment(g104,g106)
    c: InternalAlignment(g105,g106)
    c: InternalAlignment(g107,g106)
    c: InternalAlignment(g108,g106)
    c: Weight(g109) = 1
    c: Equal(g109,g110)
    c: Equal(g109,g111)
    c: InternalAlignment(g109,g112)
    c: InternalAlignment(g110,g112)
    c: InternalAlignment(g111,g112)
    c: InternalAlignment(g113,g112)
    c: InternalAlignment(g114,g112)
    c: Block(g106)
    c: Block(g112)
    c: Coincident(g115,g106)
    c: Coincident(g115,g112)
    c: Vertical(g115)
    c: Coincident(g116,g112)
    c: Coincident(g116,g70)
    c: Coincident(g117,g70)
    c: Coincident(g117,g106)
    c: Weight(g118) = 1
    c: Equal(g118,g119)
    c: Equal(g118,g120)
    c: InternalAlignment(g118,g121)
    c: InternalAlignment(g119,g121)
    c: InternalAlignment(g120,g121)
    c: InternalAlignment(g122,g121)
    c: InternalAlignment(g123,g121)
    c: Weight(g124) = 1
    c: Equal(g124,g125)
    c: Equal(g124,g126)
    c: InternalAlignment(g124,g127)
    c: InternalAlignment(g125,g127)
    c: InternalAlignment(g126,g127)
    c: InternalAlignment(g128,g127)
    c: InternalAlignment(g129,g127)
    c: Block(g121)
    c: Block(g127)
    c: Coincident(g130,g121)
    c: Coincident(g130,g127)
    c: Vertical(g130)
    c: Coincident(g131,g127)
    c: Coincident(g131,g64)
    c: Coincident(g132,g64)
    c: Coincident(g132,g121)
    c: Weight(g133) = 1
    c: Equal(g133,g134)
    c: Equal(g133,g135)
    c: InternalAlignment(g133,g136)
    c: InternalAlignment(g134,g136)
    c: InternalAlignment(g135,g136)
    c: InternalAlignment(g137,g136)
    c: InternalAlignment(g138,g136)
    c: Weight(g139) = 1
    c: Equal(g139,g140)
    c: Equal(g139,g141)
    c: InternalAlignment(g139,g142)
    c: InternalAlignment(g140,g142)
    c: InternalAlignment(g141,g142)
    c: InternalAlignment(g143,g142)
    c: InternalAlignment(g144,g142)
    c: Weight(g145) = 1
    c: Equal(g145,g146)
    c: Equal(g145,g147)
    c: InternalAlignment(g145,g148)
    c: InternalAlignment(g146,g148)
    c: InternalAlignment(g147,g148)
    c: InternalAlignment(g149,g148)
    c: InternalAlignment(g150,g148)
    c: Weight(g151) = 1
    c: Equal(g151,g152)
    c: Equal(g151,g153)
    c: InternalAlignment(g151,g154)
    c: InternalAlignment(g152,g154)
    c: InternalAlignment(g153,g154)
    c: InternalAlignment(g155,g154)
    c: InternalAlignment(g156,g154)
    c: Block(g154)
    c: Block(g148)
    c: Block(g142)
    c: Block(g136)
    c: Coincident(g157,g31)
    c: Coincident(g157,g154)
    c: Coincident(g158,g154)
    c: Coincident(g158,g148)
    c: Horizontal(g158)
    c: Coincident(g159,g148)
    c: Coincident(g159,g31)
    c: Vertical(g159)
    c: Coincident(g160,g25)
    c: Coincident(g160,g142)
    c: Vertical(g160)
    c: Coincident(g161,g142)
    c: Coincident(g161,g136)
    c: Horizontal(g161)
    c: Coincident(g162,g136)
    c: Coincident(g162,g25)
    c: Weight(g163) = 1
    c: Equal(g163,g164)
    c: Equal(g163,g165)
    c: InternalAlignment(g163,g166)
    c: InternalAlignment(g164,g166)
    c: InternalAlignment(g165,g166)
    c: InternalAlignment(g167,g166)
    c: InternalAlignment(g168,g166)
    c: Weight(g169) = 1
    c: Equal(g169,g170)
    c: Equal(g169,g171)
    c: InternalAlignment(g169,g172)
    c: InternalAlignment(g170,g172)
    c: InternalAlignment(g171,g172)
    c: InternalAlignment(g173,g172)
    c: InternalAlignment(g174,g172)
    c: Weight(g175) = 1
    c: Equal(g175,g176)
    c: Equal(g175,g177)
    c: InternalAlignment(g175,g178)
    c: InternalAlignment(g176,g178)
    c: InternalAlignment(g177,g178)
    c: InternalAlignment(g179,g178)
    c: InternalAlignment(g180,g178)
    c: Weight(g181) = 1
    c: Equal(g181,g182)
    c: Equal(g181,g183)
    c: InternalAlignment(g181,g184)
    c: InternalAlignment(g182,g184)
    c: InternalAlignment(g183,g184)
    c: InternalAlignment(g185,g184)
    c: InternalAlignment(g186,g184)
    c: Block(g184)
    c: Block(g178)
    c: Block(g172)
    c: Block(g166)
    c: Coincident(g187,g184)
    c: Coincident(g187,g178)
    c: Horizontal(g187)
    c: Coincident(g188,g178)
    c: Coincident(g188,g13)
    c: Vertical(g188)
    c: Coincident(g189,g19)
    c: Coincident(g189,g172)
    c: Vertical(g189)
    c: Coincident(g190,g172)
    c: Coincident(g190,g166)
    c: Horizontal(g190)
    c: Coincident(g191,g166)
    c: Coincident(g191,g19)
    c: Coincident(g192,g13)
    c: Weight(g193) = 1
    c: Equal(g193,g194)
    c: Equal(g193,g195)
    c: InternalAlignment(g193,g196)
    c: InternalAlignment(g194,g196)
    c: InternalAlignment(g195,g196)
    c: InternalAlignment(g197,g196)
    c: InternalAlignment(g198,g196)
    c: Weight(g199) = 1
    c: Equal(g199,g200)
    c: Equal(g199,g201)
    c: InternalAlignment(g199,g202)
    c: InternalAlignment(g200,g202)
    c: InternalAlignment(g201,g202)
    c: InternalAlignment(g203,g202)
    c: InternalAlignment(g204,g202)
    c: Block(g202)
    c: Block(g196)
    c: Coincident(g205,g202)
    c: Coincident(g205,g37)
    c: Coincident(g206,g37)
    c: Coincident(g206,g196)
    c: Coincident(g207,g196)
    c: Coincident(g207,g202)
    c: Vertical(g207)
    c: Weight(g208) = 1
    c: Equal(g208,g209)
    c: Equal(g208,g210)
    c: InternalAlignment(g208,g211)
    c: InternalAlignment(g209,g211)
    c: InternalAlignment(g210,g211)
    c: InternalAlignment(g212,g211)
    c: InternalAlignment(g213,g211)
    c: Weight(g214) = 1
    c: Equal(g214,g215)
    c: Equal(g214,g216)
    c: InternalAlignment(g214,g217)
    c: InternalAlignment(g215,g217)
    c: InternalAlignment(g216,g217)
    c: InternalAlignment(g218,g217)
    c: InternalAlignment(g219,g217)
    c: Block(g217)
    c: Block(g211)
    c: Coincident(g220,g211)
    c: Coincident(g220,g43)
    c: Coincident(g221,g43)
    c: Coincident(g221,g217)
    c: Coincident(g222,g217)
    c: Coincident(g222,g211)
    c: Vertical(g222)
    c: Horizontal(g223)
    c: Block(g223)
    c: Vertical(g224)
    c: Block(g224)
    c: Block(g225)
    c: Weight(g226) = 1
    c: Equal(g226,g227)
    c: Equal(g226,g228)
    c: InternalAlignment(g226,g229)
    c: InternalAlignment(g227,g229)
    c: InternalAlignment(g228,g229)
    c: InternalAlignment(g230,g229)
    c: InternalAlignment(g231,g229)
    c: Weight(g232) = 1
    c: Equal(g232,g233)
    c: Equal(g232,g234)
    c: InternalAlignment(g232,g235)
    c: InternalAlignment(g233,g235)
    c: InternalAlignment(g234,g235)
    c: InternalAlignment(g236,g235)
    c: InternalAlignment(g237,g235)
    c: Weight(g238) = 1
    c: Equal(g238,g239)
    c: Equal(g238,g240)
    c: InternalAlignment(g238,g241)
    c: InternalAlignment(g239,g241)
    c: InternalAlignment(g240,g241)
    c: InternalAlignment(g242,g241)
    c: InternalAlignment(g243,g241)
    c: Weight(g244) = 1
    c: Equal(g244,g245)
    c: Equal(g244,g246)
    c: InternalAlignment(g244,g247)
    c: InternalAlignment(g245,g247)
    c: InternalAlignment(g246,g247)
    c: InternalAlignment(g248,g247)
    c: InternalAlignment(g249,g247)
    c: Block(g229)
    c: Block(g235)
    c: Block(g241)
    c: Block(g247)
    c: Coincident(g250,g235)
    c: Coincident(g250,g229)
    c: Horizontal(g250)
    c: Block(g192)
    c: Weight(g251) = 1
    c: Equal(g251,g252)
    c: Equal(g251,g253)
    c: InternalAlignment(g251,g254)
    c: InternalAlignment(g252,g254)
    c: InternalAlignment(g253,g254)
    c: InternalAlignment(g255,g254)
    c: InternalAlignment(g256,g254)
    c: Weight(g257) = 1
    c: Equal(g257,g258)
    c: Equal(g257,g259)
    c: InternalAlignment(g257,g260)
    c: InternalAlignment(g258,g260)
    c: InternalAlignment(g259,g260)
    c: InternalAlignment(g261,g260)
    c: InternalAlignment(g262,g260)
    c: Block(g254)
    c: Block(g260)
    c: Coincident(g263,g254)
    c: Coincident(g263,g260)
    c: Weight(g264) = 1
    c: Equal(g264,g265)
    c: Equal(g264,g266)
    c: InternalAlignment(g264,g267)
    c: InternalAlignment(g265,g267)
    c: InternalAlignment(g266,g267)
    c: InternalAlignment(g268,g267)
    c: InternalAlignment(g269,g267)
    c: Weight(g270) = 1
    c: Equal(g270,g271)
    c: Equal(g270,g272)
    c: InternalAlignment(g270,g273)
    c: InternalAlignment(g271,g273)
    c: InternalAlignment(g272,g273)
    c: InternalAlignment(g274,g273)
    c: InternalAlignment(g275,g273)
    c: Weight(g276) = 1
    c: Equal(g276,g277)
    c: Equal(g276,g278)
    c: InternalAlignment(g276,g279)
    c: InternalAlignment(g277,g279)
    c: InternalAlignment(g278,g279)
    c: InternalAlignment(g280,g279)
    c: InternalAlignment(g281,g279)
    c: Block(g279)
    c: Block(g273)
    c: Block(g267)
    c: Coincident(g282,g273)
    c: Coincident(g282,g267)
    c: Coincident(g283,g267)
    c: Coincident(g283,g279)
    c: Vertical(g283)
    c: Coincident(g284,g279)
    c: Coincident(g284,g273)
    c: Horizontal(g284)
    c: Weight(g285) = 1
    c: Equal(g285,g286)
    c: InternalAlignment(g285,g287)
    c: InternalAlignment(g286,g287)
    c: InternalAlignment(g288,g287)
    c: InternalAlignment(g289,g287)
    c: Weight(g290) = 1
    c: InternalAlignment(g291,g293)
    c: InternalAlignment(g292,g293)
    c: InternalAlignment(g294,g293)
    c: InternalAlignment(g295,g293)
    c: Weight(g296) = 1
    c: Equal(g296,g297)
    c: Equal(g296,g298)
    c: InternalAlignment(g296,g299)
    c: InternalAlignment(g297,g299)
    c: InternalAlignment(g298,g299)
    c: InternalAlignment(g300,g299)
    c: InternalAlignment(g301,g299)
    c: Equal(g302,g303)
    c: Equal(g302,g304)
    c: InternalAlignment(g302,g305)
    c: InternalAlignment(g303,g305)
    c: InternalAlignment(g304,g305)
    c: InternalAlignment(g306,g305)
    c: InternalAlignment(g307,g305)
    c: Block(g293)
    c: Block(g299)
    c: Block(g305)
    c: Block(g287)
    c: Coincident(g308,g287)
    c: Coincident(g308,g293)
    c: Horizontal(g308)
    c: Coincident(g309,g293)
    c: Coincident(g309,g299)
    c: Vertical(g309)
    c: Coincident(g310,g299)
    c: Coincident(g310,g305)
    c: Horizontal(g310)
    c: Coincident(g311,g305)
    c: Coincident(g311,g287)
    c: Weight(g312) = 1
    c: Equal(g312,g313)
    c: Equal(g312,g314)
    c: InternalAlignment(g312,g315)
    c: InternalAlignment(g313,g315)
    c: InternalAlignment(g314,g315)
    c: InternalAlignment(g316,g315)
    c: InternalAlignment(g317,g315)
    c: Weight(g318) = 1
    c: Equal(g318,g319)
    c: Equal(g318,g320)
    c: InternalAlignment(g318,g321)
    c: InternalAlignment(g319,g321)
    c: InternalAlignment(g320,g321)
    c: InternalAlignment(g322,g321)
    c: InternalAlignment(g323,g321)
    c: Weight(g324) = 1
    c: Equal(g324,g325)
    c: Equal(g324,g326)
    c: InternalAlignment(g324,g327)
    c: InternalAlignment(g325,g327)
    c: InternalAlignment(g326,g327)
    c: InternalAlignment(g328,g327)
    c: InternalAlignment(g329,g327)
    c: Block(g327)
    c: Block(g321)
    c: Block(g315)
    c: Coincident(g330,g327)
    c: Coincident(g330,g321)
    c: Horizontal(g330)
    c: Coincident(g331,g321)
    c: Coincident(g331,g315)
    c: Vertical(g331)
    c: Coincident(g332,g315)
    c: Coincident(g332,g327)
    c: InternalAlignment(g333,g334)
    c: InternalAlignment(g335,g334)
    c: InternalAlignment(g336,g334)
    c: Block(g334)
    c: Equal(g337,g338)
    c: Equal(g337,g339)
    c: InternalAlignment(g337,g340)
    c: InternalAlignment(g338,g340)
    c: InternalAlignment(g339,g340)
    c: InternalAlignment(g341,g340)
    c: InternalAlignment(g342,g340)
    c: Block(g340)
    c: Coincident(g343,g334)
    c: Horizontal(g343)
    c: Block(g343)
    c: Coincident(g344,g334)
    c: Coincident(g344,g260)
    c: Vertical(g344)
    c: Coincident(g345,g340)
    c: Coincident(g345,g254)
    c: Vertical(g345)
    c: Coincident(g347,g5)
    c: Coincident(g348,g5)
    c: Block(g346)
    c: Block(g5)
    c: Block(g348)
    c: Block(g347)
    c: Distance(g344) = 119.89
FEATURE [Sketcher::SketchObject] Sketch001
  FullyConstrained = true
  MapMode = 4
  Placement = pos=(0,0,0) rot=(0.57735,0.57735,0.57735;2.0944rad)
  Support = -> [Sketch]
  sketch-geometry (46):
    g0: BSplineCurve PolesCount=3 KnotsCount=2 Degree=2 IsPeriodic=0
    g1: ArcOfCircle CenterX=73.1223 CenterY=-32.291 CenterZ=0 NormalX=0 NormalY=0 NormalZ=1 AngleXU=0 Radius=13 StartAngle=5.92268 EndAngle=9.06428
    g2: ArcOfCircle CenterX=66.7816 CenterY=-49.1439 CenterZ=0 NormalX=0 NormalY=0 NormalZ=1 AngleXU=0 Radius=13 StartAngle=2.78068 EndAngle=5.92131
    g3: ArcOfCircle CenterX=55.9263 CenterY=-78.1807 CenterZ=0 NormalX=0 NormalY=0 NormalZ=1 AngleXU=0 Radius=13 StartAngle=5.92268 EndAngle=9.06428
    g4: ArcOfCircle CenterX=49.5884 CenterY=-95.0342 CenterZ=0 NormalX=0 NormalY=0 NormalZ=1 AngleXU=0 Radius=13 StartAngle=2.78068 EndAngle=5.92131
    g5: ArcOfCircle CenterX=38.7206 CenterY=-124.067 CenterZ=0 NormalX=0 NormalY=0 NormalZ=1 AngleXU=0 Radius=13 StartAngle=5.92268 EndAngle=9.06428
    g6: ArcOfCircle CenterX=32.3875 CenterY=-140.92 CenterZ=0 NormalX=0 NormalY=0 NormalZ=1 AngleXU=0 Radius=13 StartAngle=2.78068 EndAngle=5.92131
    g7: ArcOfCircle CenterX=21.4715 CenterY=-169.934 CenterZ=0 NormalX=0 NormalY=0 NormalZ=1 AngleXU=0 Radius=13 StartAngle=5.92268 EndAngle=9.06428
    g8: ArcOfCircle CenterX=15.1336 CenterY=-186.787 CenterZ=0 NormalX=0 NormalY=0 NormalZ=1 AngleXU=0 Radius=13 StartAngle=2.78068 EndAngle=5.92131
    g9-g12: Circle x4 (B-spline internal-alignment scaffolding for g13; pole/knot coordinates omitted)
    g13: BSplineCurve PolesCount=4 KnotsCount=2 Degree=3 IsPeriodic=0
    g14: GeomPoint X=28.8094 Y=-19.0875 Z=0
    g15: GeomPoint X=47.0443 Y=-50.4712 Z=0
    g16: Circle CenterX=53.5586 CenterY=-23.2695 CenterZ=0 NormalX=0 NormalY=0 NormalZ=1 AngleXU=0 Radius=3.24518
    g17: Circle CenterX=-195.441 CenterY=-127.082 CenterZ=0 NormalX=0 NormalY=0 NormalZ=1 AngleXU=0 Radius=1
    g18: Circle CenterX=-8.24091 CenterY=-197.481 CenterZ=0 NormalX=0 NormalY=0 NormalZ=1 AngleXU=0 Radius=1
    g19: Circle CenterX=12.8789 CenterY=-141.321 CenterZ=0 NormalX=0 NormalY=0 NormalZ=1 AngleXU=0 Radius=1
    g20: BSplineCurve PolesCount=3 KnotsCount=2 Degree=2 IsPeriodic=0
    g21: GeomPoint X=-195.441 Y=-127.082 Z=0
    g22: GeomPoint X=12.8789 Y=-141.321 Z=0
    g23: Circle CenterX=-12.8016 CenterY=-179.036 CenterZ=0 NormalX=0 NormalY=0 NormalZ=1 AngleXU=0 Radius=10.5072
    g24: Circle CenterX=0.933922 CenterY=-166.43 CenterZ=0 NormalX=0 NormalY=0 NormalZ=1 AngleXU=0 Radius=3.26661
    g25: Circle CenterX=-33.5518 CenterY=-176.44 CenterZ=0 NormalX=0 NormalY=0 NormalZ=1 AngleXU=0 Radius=5.64388
    g26: Circle CenterX=-47.2366 CenterY=-173.859 CenterZ=0 NormalX=0 NormalY=0 NormalZ=1 AngleXU=0 Radius=3.01653
    g27: Circle CenterX=-56.2595 CenterY=-171.456 CenterZ=0 NormalX=0 NormalY=0 NormalZ=1 AngleXU=0 Radius=2.12826
    g28: ArcOfCircle CenterX=51.2151 CenterY=-198.473 CenterZ=0 NormalX=0 NormalY=0 NormalZ=1 AngleXU=0 Radius=20 StartAngle=2.78189 EndAngle=4.35269
    g29: LineSegment StartX=32.4951 StartY=-191.433 StartZ=0 EndX=94.6578 EndY=-26.1352 EndZ=0
    g30: LineSegment StartX=43.1192 StartY=-220.001 StartZ=0 EndX=-196.497 EndY=-129.89 EndZ=0
    g31: LineSegment StartX=43.1192 StartY=-220.001 StartZ=0 EndX=44.1752 EndY=-217.193 EndZ=0
    g32: LineSegment StartX=117.223 StartY=-19.0875 StartZ=0 EndX=117.223 EndY=-16.0875 EndZ=0
    g33: LineSegment StartX=117.223 StartY=-16.0875 StartZ=0 EndX=17.2232 EndY=-16.0875 EndZ=0
    g34: LineSegment StartX=17.2232 StartY=-16.0875 StartZ=0 EndX=17.2232 EndY=-19.0875 EndZ=0
    g35: LineSegment StartX=28.8094 StartY=-19.0875 StartZ=0 EndX=17.2232 EndY=-19.0875 EndZ=0
    g36: LineSegment StartX=47.0443 StartY=-50.4712 StartZ=0 EndX=12.8789 EndY=-141.321 EndZ=0
    g37: LineSegment StartX=-195.441 StartY=-127.082 StartZ=0 EndX=-196.497 EndY=-129.89 EndZ=0
    g38: LineSegment StartX=85.2866 StartY=-36.8766 StartZ=0 EndX=78.9396 EndY=-53.7463 EndZ=0
    g39: LineSegment StartX=60.9579 StartY=-27.7053 StartZ=0 EndX=54.6191 EndY=-44.5532 EndZ=0
    g40: LineSegment StartX=68.0907 StartY=-82.7664 StartZ=0 EndX=61.7465 EndY=-99.6365 EndZ=0
    g41: LineSegment StartX=43.7619 StartY=-73.595 StartZ=0 EndX=37.426 EndY=-90.4435 EndZ=0
    g42: LineSegment StartX=50.885 StartY=-128.652 StartZ=0 EndX=44.5456 EndY=-145.522 EndZ=0
    g43: LineSegment StartX=26.5562 StartY=-119.481 StartZ=0 EndX=20.2251 EndY=-136.329 EndZ=0
    g44: LineSegment StartX=9.3071 StartY=-165.349 StartZ=0 EndX=2.97115 EndY=-182.197 EndZ=0
    g45: LineSegment StartX=33.6358 StartY=-174.52 StartZ=0 EndX=27.2917 EndY=-191.39 EndZ=0
  constraints (71):
    c: Block(g0)
    c: Block(g1)
    c: Block(g2)
    c: Block(g4)
    c: Block(g3)
    c: Block(g6)
    c: Block(g5)
    c: Block(g8)
    c: Block(g7)
    c: Weight(g9) = 1
    c: Equal(g9,g10)
    c: Equal(g9,g11)
    c: Equal(g9,g12)
    c: InternalAlignment(g9-g12 -> g13) x4
    c: InternalAlignment(g14,g13)
    c: InternalAlignment(g15,g13)
    c: Block(g16)
    c: Weight(g17) = 1
    c: Equal(g17,g18)
    c: Equal(g17,g19)
    c: InternalAlignment(g17,g20)
    c: InternalAlignment(g18,g20)
    c: InternalAlignment(g19,g20)
    c: InternalAlignment(g21,g20)
    c: InternalAlignment(g22,g20)
    c: Block(g20)
    c: Block(g23)
    c: Block(g24)
    c: Block(g25)
    c: Block(g26)
    c: Block(g27)
    c: Block(g28)
    c: Coincident(g29,g28)
    c: Coincident(g29,g0)
    c: Block(g13)
    c: Coincident(g31,g30)
    c: Coincident(g31,g28)
    c: Block(g31)
    c: Coincident(g32,g0)
    c: Vertical(g32)
    c: Coincident(g33,g32)
    c: Horizontal(g33)
    c: Coincident(g34,g33)
    c: Vertical(g34)
    c: Block(g33)
    c: Coincident(g35,g13)
    c: Coincident(g35,g34)
    c: Horizontal(g35)
    c: Coincident(g36,g13)
    c: Coincident(g36,g20)
    c: Coincident(g37,g20)
    c: Coincident(g37,g30)
    c: Block(g30)
    c: Coincident(g38,g1)
    c: Coincident(g38,g2)
    c: Coincident(g39,g1)
    c: Coincident(g39,g2)
    c: Coincident(g40,g3)
    c: Coincident(g40,g4)
    c: Coincident(g41,g3)
    c: Coincident(g41,g4)
    c: Coincident(g42,g5)
    c: Coincident(g42,g6)
    c: Coincident(g43,g5)
    c: Coincident(g43,g6)
    c: Coincident(g44,g7)
    c: Coincident(g44,g8)
    c: Coincident(g45,g7)
    c: Coincident(g45,g8)
    c: Distance(g30) = 256
    c: Distance(g33) = 100
FEATURE [Part::Extrusion] Extrude002
  Base = -> Sketch001
  Dir = (1,0,0)
  DirMode = 2
  FaceMakerClass = Part::FaceMakerBullseye
  LengthFwd = 8
  LengthRev = 0
  Solid = true
  Symmetric = false
FEATURE [Sketcher::SketchObject] Sketch002
  FullyConstrained = true
  sketch-geometry (20):
    g0: LineSegment StartX=-2.77179 StartY=-200.304 StartZ=0 EndX=5.22821 EndY=-200.304 EndZ=0
    g1: LineSegment StartX=5.22821 StartY=-200.304 StartZ=0 EndX=5.22821 EndY=-197.304 EndZ=0
    g2: LineSegment StartX=-2.77179 StartY=-200.304 StartZ=0 EndX=-2.77179 EndY=-197.304 EndZ=0
    g3: LineSegment StartX=5.22821 StartY=-197.304 StartZ=0 EndX=8.22821 EndY=-197.304 EndZ=0
    g4: LineSegment StartX=-2.77179 StartY=-197.304 StartZ=0 EndX=-5.77179 EndY=-197.304 EndZ=0
    g5: LineSegment StartX=19.2282 StartY=-203.304 StartZ=0 EndX=19.2282 EndY=-206.304 EndZ=0
    g6: LineSegment StartX=-16.7718 StartY=-203.304 StartZ=0 EndX=-16.7718 EndY=-206.304 EndZ=0
    g7: LineSegment StartX=-16.7718 StartY=-206.304 StartZ=0 EndX=19.2282 EndY=-206.304 EndZ=0
    g8: Circle CenterX=-16.7718 CenterY=-203.304 CenterZ=0 NormalX=0 NormalY=0 NormalZ=1 AngleXU=0 Radius=1
    g9: Circle CenterX=-5.77179 CenterY=-203.304 CenterZ=0 NormalX=0 NormalY=0 NormalZ=1 AngleXU=0 Radius=1
    g10: Circle CenterX=-5.77179 CenterY=-197.304 CenterZ=0 NormalX=0 NormalY=0 NormalZ=1 AngleXU=0 Radius=1
    g11: BSplineCurve PolesCount=3 KnotsCount=2 Degree=2 IsPeriodic=0
    g12: GeomPoint X=-16.7718 Y=-203.304 Z=0
    g13: GeomPoint X=-5.77179 Y=-197.304 Z=0
    g14: Circle CenterX=19.2282 CenterY=-203.304 CenterZ=0 NormalX=0 NormalY=0 NormalZ=1 AngleXU=0 Radius=1
    g15: Circle CenterX=8.22821 CenterY=-203.304 CenterZ=0 NormalX=0 NormalY=0 NormalZ=1 AngleXU=0 Radius=1
    g16: Circle CenterX=8.22821 CenterY=-197.304 CenterZ=0 NormalX=0 NormalY=0 NormalZ=1 AngleXU=0 Radius=1
    g17: BSplineCurve PolesCount=3 KnotsCount=2 Degree=2 IsPeriodic=0
    g18: GeomPoint X=19.2282 Y=-203.304 Z=0
    g19: GeomPoint X=8.22821 Y=-197.304 Z=0
  constraints (41):
    c: Horizontal(g0)
    c: Distance(g0) = 8
    c: Coincident(g1,g0)
    c: Vertical(g1)
    c: Distance(g1) = 3
    c: Coincident(g2,g0)
    c: Vertical(g2)
    c: Distance(g2) = 3
    c: Coincident(g3,g1)
    c: Horizontal(g3)
    c: Distance(g3) = 3
    c: Coincident(g4,g2)
    c: Horizontal(g4)
    c: Distance(g4) = 3
    c: Vertical(g5)
    c: Vertical(g6)
    c: Coincident(g7,g6)
    c: Coincident(g7,g5)
    c: Weight(g8) = 1
    c: Equal(g8,g9)
    c: Equal(g8,g10)
    c: Coincident(g11,g4)
    c: InternalAlignment(g8,g11)
    c: InternalAlignment(g9,g11)
    c: InternalAlignment(g10,g11)
    c: InternalAlignment(g12,g11)
    c: InternalAlignment(g13,g11)
    c: Coincident(g17,g5)
    c: Weight(g14) = 1
    c: Equal(g14,g15)
    c: Equal(g14,g16)
    c: Coincident(g17,g3)
    c: InternalAlignment(g14,g17)
    c: InternalAlignment(g15,g17)
    c: InternalAlignment(g16,g17)
    c: InternalAlignment(g18,g17)
    c: InternalAlignment(g19,g17)
    c: Block(g7)
    c: Block(g17)
    c: Block(g11)
    c: Block(g6)
FEATURE [Part::Extrusion] Extrude003
  Base = -> Sketch002
  Dir = (0,0,1)
  DirMode = 2
  FaceMakerClass = Part::FaceMakerBullseye
  LengthFwd = 260
  LengthRev = 0
  Solid = true
  Symmetric = false
FEATURE [Part::Extrusion] Extrude
  Base = -> Sketch
  Dir = (0,0,1)
  DirMode = 2
  FaceMakerClass = Part::FaceMakerBullseye
  LengthFwd = 14
  LengthRev = 0
  Solid = true
  Symmetric = false
FEATURE [Sketcher::SketchObject] Sketch003
  FullyConstrained = false
  sketch-geometry (351):
    g0: LineSegment StartX=-10.9272 StartY=-82.7794 StartZ=0 EndX=46.0728 EndY=-51.4823 EndZ=0
    g1: LineSegment StartX=-10.9272 StartY=76.4095 StartZ=0 EndX=-10.9272 EndY=-82.7794 EndZ=0
    g2: LineSegment StartX=46.0728 StartY=76.4095 StartZ=0 EndX=46.0728 EndY=-51.4823 EndZ=0
    g3: LineSegment StartX=-42.9272 StartY=136.221 StartZ=0 EndX=-42.9272 EndY=-103.779 EndZ=0
    g4: LineSegment StartX=407.073 StartY=136.221 StartZ=0 EndX=407.073 EndY=-103.779 EndZ=0
    g5: ArcOfCircle CenterX=-26.9272 CenterY=-83.7794 CenterZ=0 NormalX=0 NormalY=0 NormalZ=1 AngleXU=0 Radius=8 StartAngle=3.14159 EndAngle=6.28319
    g6: ArcOfCircle CenterX=391.073 CenterY=22.1087 CenterZ=0 NormalX=0 NormalY=0 NormalZ=1 AngleXU=0 Radius=8 StartAngle=-4.4e-15 EndAngle=3.14159
    g7: LineSegment StartX=399.073 StartY=22.1087 StartZ=0 EndX=399.073 EndY=-83.7794 EndZ=0
    g8: LineSegment StartX=383.073 StartY=22.1087 StartZ=0 EndX=383.073 EndY=-83.7794 EndZ=0
    g9: ArcOfCircle CenterX=391.073 CenterY=-83.7794 CenterZ=0 NormalX=0 NormalY=0 NormalZ=1 AngleXU=0 Radius=8 StartAngle=3.14159 EndAngle=6.28319
    g10: Circle CenterX=175.022 CenterY=27.0628 CenterZ=0 NormalX=0 NormalY=0 NormalZ=1 AngleXU=0 Radius=1
    g11: Circle CenterX=179.022 CenterY=24.8665 CenterZ=0 NormalX=0 NormalY=0 NormalZ=1 AngleXU=0 Radius=1
    g12: Circle CenterX=179.022 CenterY=27.0628 CenterZ=0 NormalX=0 NormalY=0 NormalZ=1 AngleXU=0 Radius=1
    g13: BSplineCurve PolesCount=3 KnotsCount=2 Degree=2 IsPeriodic=0
    g14: GeomPoint X=175.022 Y=27.0628 Z=0
    g15: GeomPoint X=179.022 Y=27.0628 Z=0
    g16: Circle CenterX=189.124 CenterY=27.0628 CenterZ=0 NormalX=0 NormalY=0 NormalZ=1 AngleXU=0 Radius=1
    g17: Circle CenterX=185.124 CenterY=24.8665 CenterZ=0 NormalX=0 NormalY=0 NormalZ=1 AngleXU=0 Radius=1
    g18: Circle CenterX=185.124 CenterY=27.0628 CenterZ=0 NormalX=0 NormalY=0 NormalZ=1 AngleXU=0 Radius=1
    g19: BSplineCurve PolesCount=3 KnotsCount=2 Degree=2 IsPeriodic=0
    g20: GeomPoint X=189.124 Y=27.0628 Z=0
    g21: GeomPoint X=185.124 Y=27.0628 Z=0
    g22: Circle CenterX=175.022 CenterY=5.37834 CenterZ=0 NormalX=0 NormalY=0 NormalZ=1 AngleXU=0 Radius=1
    g23: Circle CenterX=179.022 CenterY=7.57463 CenterZ=0 NormalX=0 NormalY=0 NormalZ=1 AngleXU=0 Radius=1
    g24: Circle CenterX=179.022 CenterY=5.34704 CenterZ=0 NormalX=0 NormalY=0 NormalZ=1 AngleXU=0 Radius=1
    g25: BSplineCurve PolesCount=3 KnotsCount=2 Degree=2 IsPeriodic=0
    g26: GeomPoint X=175.022 Y=5.37834 Z=0
    g27: GeomPoint X=179.022 Y=5.34704 Z=0
    g28: Circle CenterX=189.124 CenterY=5.37834 CenterZ=0 NormalX=0 NormalY=0 NormalZ=1 AngleXU=0 Radius=1
    g29: Circle CenterX=185.124 CenterY=7.57463 CenterZ=0 NormalX=0 NormalY=0 NormalZ=1 AngleXU=0 Radius=1
    g30: Circle CenterX=185.124 CenterY=5.34704 CenterZ=0 NormalX=0 NormalY=0 NormalZ=1 AngleXU=0 Radius=1
    g31: BSplineCurve PolesCount=3 KnotsCount=2 Degree=2 IsPeriodic=0
    g32: GeomPoint X=189.124 Y=5.37834 Z=0
    g33: GeomPoint X=185.124 Y=5.34704 Z=0
    g34: Circle CenterX=165.871 CenterY=18.1458 CenterZ=0 NormalX=0 NormalY=0 NormalZ=1 AngleXU=0 Radius=1
    g35: Circle CenterX=169.377 CenterY=16.2206 CenterZ=0 NormalX=0 NormalY=0 NormalZ=1 AngleXU=0 Radius=1
    g36: Circle CenterX=165.871 CenterY=14.2954 CenterZ=0 NormalX=0 NormalY=0 NormalZ=1 AngleXU=0 Radius=1
    g37: BSplineCurve PolesCount=3 KnotsCount=2 Degree=2 IsPeriodic=0
    g38: GeomPoint X=165.871 Y=18.1458 Z=0
    g39: GeomPoint X=165.871 Y=14.2954 Z=0
    g40: Circle CenterX=198.275 CenterY=18.1458 CenterZ=0 NormalX=0 NormalY=0 NormalZ=1 AngleXU=0 Radius=1
    g41: Circle CenterX=194.768 CenterY=16.2206 CenterZ=0 NormalX=0 NormalY=0 NormalZ=1 AngleXU=0 Radius=1
    g42: Circle CenterX=198.275 CenterY=14.2954 CenterZ=0 NormalX=0 NormalY=0 NormalZ=1 AngleXU=0 Radius=1
    g43: BSplineCurve PolesCount=3 KnotsCount=2 Degree=2 IsPeriodic=0
    g44: GeomPoint X=198.275 Y=18.1458 Z=0
    g45: GeomPoint X=198.275 Y=14.2954 Z=0
    g46: LineSegment StartX=407.073 StartY=-103.779 StartZ=0 EndX=-42.9272 EndY=-103.779 EndZ=0
    g47: LineSegment StartX=407.073 StartY=136.221 StartZ=0 EndX=-42.9272 EndY=136.221 EndZ=0
    g48: LineSegment StartX=46.0728 StartY=76.4095 StartZ=0 EndX=-10.9272 EndY=76.4095 EndZ=0
    g49: Circle CenterX=125.607 CenterY=54.1951 CenterZ=0 NormalX=0 NormalY=0 NormalZ=1 AngleXU=0 Radius=1
    g50: Circle CenterX=139.632 CenterY=46.4944 CenterZ=0 NormalX=0 NormalY=0 NormalZ=1 AngleXU=0 Radius=1
    g51: Circle CenterX=127.326 CenterY=56.7187 CenterZ=0 NormalX=0 NormalY=0 NormalZ=1 AngleXU=0 Radius=1
    g52: BSplineCurve PolesCount=3 KnotsCount=2 Degree=2 IsPeriodic=0
    g53: GeomPoint X=125.607 Y=54.1951 Z=0
    g54: GeomPoint X=127.326 Y=56.7187 Z=0
    g55: Circle CenterX=236.821 CenterY=56.7187 CenterZ=0 NormalX=0 NormalY=0 NormalZ=1 AngleXU=0 Radius=1
    g56: Circle CenterX=224.513 CenterY=46.4944 CenterZ=0 NormalX=0 NormalY=0 NormalZ=1 AngleXU=0 Radius=1
    g57: Circle CenterX=238.538 CenterY=54.1951 CenterZ=0 NormalX=0 NormalY=0 NormalZ=1 AngleXU=0 Radius=1
    g58: BSplineCurve PolesCount=3 KnotsCount=2 Degree=2 IsPeriodic=0
    g59: GeomPoint X=236.821 Y=56.7187 Z=0
    g60: GeomPoint X=238.538 Y=54.1951 Z=0
    g61: Circle CenterX=238.538 CenterY=-21.7539 CenterZ=0 NormalX=0 NormalY=0 NormalZ=1 AngleXU=0 Radius=1
    g62: Circle CenterX=224.513 CenterY=-14.0532 CenterZ=0 NormalX=0 NormalY=0 NormalZ=1 AngleXU=0 Radius=1
    g63: Circle CenterX=236.821 CenterY=-24.2775 CenterZ=0 NormalX=0 NormalY=0 NormalZ=1 AngleXU=0 Radius=1
    g64: BSplineCurve PolesCount=3 KnotsCount=2 Degree=2 IsPeriodic=0
    g65: GeomPoint X=238.538 Y=-21.7539 Z=0
    g66: GeomPoint X=236.821 Y=-24.2775 Z=0
    g67: Circle CenterX=125.607 CenterY=-21.7539 CenterZ=0 NormalX=0 NormalY=0 NormalZ=1 AngleXU=0 Radius=1
    g68: Circle CenterX=139.632 CenterY=-14.0532 CenterZ=0 NormalX=0 NormalY=0 NormalZ=1 AngleXU=0 Radius=1
    g69: Circle CenterX=127.325 CenterY=-24.2775 CenterZ=0 NormalX=0 NormalY=0 NormalZ=1 AngleXU=0 Radius=1
    g70: BSplineCurve PolesCount=3 KnotsCount=2 Degree=2 IsPeriodic=0
    g71: GeomPoint X=125.607 Y=-21.7539 Z=0
    g72: GeomPoint X=127.325 Y=-24.2775 Z=0
    g73: Circle CenterX=302.996 CenterY=111.695 CenterZ=0 NormalX=0 NormalY=0 NormalZ=1 AngleXU=0 Radius=1
    g74: Circle CenterX=306.073 CenterY=114.251 CenterZ=0 NormalX=0 NormalY=0 NormalZ=1 AngleXU=0 Radius=1
    g75: Circle CenterX=306.073 CenterY=110.251 CenterZ=0 NormalX=0 NormalY=0 NormalZ=1 AngleXU=0 Radius=1
    g76: BSplineCurve PolesCount=3 KnotsCount=2 Degree=2 IsPeriodic=0
    g77: GeomPoint X=302.996 Y=111.695 Z=0
    g78: GeomPoint X=306.073 Y=110.251 Z=0
    g79: Circle CenterX=306.073 CenterY=95.2763 CenterZ=0 NormalX=0 NormalY=0 NormalZ=1 AngleXU=0 Radius=1
    g80: Circle CenterX=306.073 CenterY=91.2763 CenterZ=0 NormalX=0 NormalY=0 NormalZ=1 AngleXU=0 Radius=1
    g81: Circle CenterX=302.567 CenterY=89.3511 CenterZ=0 NormalX=0 NormalY=0 NormalZ=1 AngleXU=0 Radius=1
    g82: BSplineCurve PolesCount=3 KnotsCount=2 Degree=2 IsPeriodic=0
    g83: GeomPoint X=306.073 Y=95.2763 Z=0
    g84: GeomPoint X=302.567 Y=89.3511 Z=0
    g85: LineSegment StartX=306.073 StartY=110.251 StartZ=0 EndX=306.073 EndY=95.2763 EndZ=0
    g86: LineSegment StartX=302.996 StartY=111.695 StartZ=0 EndX=236.821 EndY=56.7187 EndZ=0
    g87: LineSegment StartX=238.538 StartY=54.1951 StartZ=0 EndX=302.567 EndY=89.3511 EndZ=0
    g88: Circle CenterX=61.1496 CenterY=111.695 CenterZ=0 NormalX=0 NormalY=0 NormalZ=1 AngleXU=0 Radius=1
    g89: Circle CenterX=58.0728 CenterY=114.251 CenterZ=0 NormalX=0 NormalY=0 NormalZ=1 AngleXU=0 Radius=1
    g90: Circle CenterX=58.0728 CenterY=110.251 CenterZ=0 NormalX=0 NormalY=0 NormalZ=1 AngleXU=0 Radius=1
    g91: BSplineCurve PolesCount=3 KnotsCount=2 Degree=2 IsPeriodic=0
    g92: GeomPoint X=61.1496 Y=111.695 Z=0
    g93: GeomPoint X=58.0728 Y=110.251 Z=0
    g94: Circle CenterX=61.5791 CenterY=89.3511 CenterZ=0 NormalX=0 NormalY=0 NormalZ=1 AngleXU=0 Radius=1
    g95: Circle CenterX=58.0728 CenterY=91.2763 CenterZ=0 NormalX=0 NormalY=0 NormalZ=1 AngleXU=0 Radius=1
    g96: Circle CenterX=58.0728 CenterY=95.2763 CenterZ=0 NormalX=0 NormalY=0 NormalZ=1 AngleXU=0 Radius=1
    g97: BSplineCurve PolesCount=3 KnotsCount=2 Degree=2 IsPeriodic=0
    g98: GeomPoint X=61.5791 Y=89.3511 Z=0
    g99: GeomPoint X=58.0728 Y=95.2763 Z=0
    g100: LineSegment StartX=58.0728 StartY=110.251 StartZ=0 EndX=58.0728 EndY=95.2763 EndZ=0
    g101: LineSegment StartX=61.1496 StartY=111.695 StartZ=0 EndX=127.326 EndY=56.7187 EndZ=0
    g102: LineSegment StartX=125.607 StartY=54.1951 StartZ=0 EndX=61.5791 EndY=89.3511 EndZ=0
    g103: Circle CenterX=61.5791 CenterY=-56.9099 CenterZ=0 NormalX=0 NormalY=0 NormalZ=1 AngleXU=0 Radius=1
    g104: Circle CenterX=58.0728 CenterY=-58.8351 CenterZ=0 NormalX=0 NormalY=0 NormalZ=1 AngleXU=0 Radius=1
    g105: Circle CenterX=58.0728 CenterY=-62.8351 CenterZ=0 NormalX=0 NormalY=0 NormalZ=1 AngleXU=0 Radius=1
    g106: BSplineCurve PolesCount=3 KnotsCount=2 Degree=2 IsPeriodic=0
    g107: GeomPoint X=61.5791 Y=-56.9099 Z=0
    g108: GeomPoint X=58.0728 Y=-62.8351 Z=0
    g109: Circle CenterX=58.0728 CenterY=-77.8102 CenterZ=0 NormalX=0 NormalY=0 NormalZ=1 AngleXU=0 Radius=1
    g110: Circle CenterX=58.0728 CenterY=-81.8102 CenterZ=0 NormalX=0 NormalY=0 NormalZ=1 AngleXU=0 Radius=1
    g111: Circle CenterX=61.1496 CenterY=-79.2541 CenterZ=0 NormalX=0 NormalY=0 NormalZ=1 AngleXU=0 Radius=1
    g112: BSplineCurve PolesCount=3 KnotsCount=2 Degree=2 IsPeriodic=0
    g113: GeomPoint X=58.0728 Y=-77.8102 Z=0
    g114: GeomPoint X=61.1496 Y=-79.2541 Z=0
    g115: LineSegment StartX=58.0728 StartY=-62.8351 StartZ=0 EndX=58.0728 EndY=-77.8102 EndZ=0
    g116: LineSegment StartX=61.1496 StartY=-79.2541 StartZ=0 EndX=127.325 EndY=-24.2775 EndZ=0
    g117: LineSegment StartX=125.607 StartY=-21.7539 StartZ=0 EndX=61.5791 EndY=-56.9099 EndZ=0
    g118: Circle CenterX=302.567 CenterY=-56.9099 CenterZ=0 NormalX=0 NormalY=0 NormalZ=1 AngleXU=0 Radius=1
    g119: Circle CenterX=306.073 CenterY=-58.8351 CenterZ=0 NormalX=0 NormalY=0 NormalZ=1 AngleXU=0 Radius=1
    g120: Circle CenterX=306.073 CenterY=-62.8351 CenterZ=0 NormalX=0 NormalY=0 NormalZ=1 AngleXU=0 Radius=1
    g121: BSplineCurve PolesCount=3 KnotsCount=2 Degree=2 IsPeriodic=0
    g122: GeomPoint X=302.567 Y=-56.9099 Z=0
    g123: GeomPoint X=306.073 Y=-62.8351 Z=0
    g124: Circle CenterX=302.996 CenterY=-79.2541 CenterZ=0 NormalX=0 NormalY=0 NormalZ=1 AngleXU=0 Radius=1
    g125: Circle CenterX=306.073 CenterY=-81.8102 CenterZ=0 NormalX=0 NormalY=0 NormalZ=1 AngleXU=0 Radius=1
    g126: Circle CenterX=306.073 CenterY=-77.8102 CenterZ=0 NormalX=0 NormalY=0 NormalZ=1 AngleXU=0 Radius=1
    g127: BSplineCurve PolesCount=3 KnotsCount=2 Degree=2 IsPeriodic=0
    g128: GeomPoint X=302.996 Y=-79.2541 Z=0
    g129: GeomPoint X=306.073 Y=-77.8102 Z=0
    g130: LineSegment StartX=306.073 StartY=-62.8351 StartZ=0 EndX=306.073 EndY=-77.8102 EndZ=0
    g131: LineSegment StartX=302.996 StartY=-79.2541 StartZ=0 EndX=236.821 EndY=-24.2775 EndZ=0
    g132: LineSegment StartX=238.538 StartY=-21.7539 StartZ=0 EndX=302.567 EndY=-56.9099 EndZ=0
    g133: Circle CenterX=61.6457 CenterY=-88.8112 CenterZ=0 NormalX=0 NormalY=0 NormalZ=1 AngleXU=0 Radius=1
    g134: Circle CenterX=58.0728 CenterY=-91.7794 CenterZ=0 NormalX=0 NormalY=0 NormalZ=1 AngleXU=0 Radius=1
    g135: Circle CenterX=63.9135 CenterY=-91.7794 CenterZ=0 NormalX=0 NormalY=0 NormalZ=1 AngleXU=0 Radius=1
    g136: BSplineCurve PolesCount=3 KnotsCount=2 Degree=2 IsPeriodic=0
    g137: GeomPoint X=61.6457 Y=-88.8112 Z=0
    g138: GeomPoint X=63.9135 Y=-91.7794 Z=0
    g139: Circle CenterX=179.022 CenterY=-85.8163 CenterZ=0 NormalX=0 NormalY=0 NormalZ=1 AngleXU=0 Radius=1
    g140: Circle CenterX=179.022 CenterY=-91.7794 CenterZ=0 NormalX=0 NormalY=0 NormalZ=1 AngleXU=0 Radius=1
    g141: Circle CenterX=171.895 CenterY=-91.7794 CenterZ=0 NormalX=0 NormalY=0 NormalZ=1 AngleXU=0 Radius=1
    g142: BSplineCurve PolesCount=3 KnotsCount=2 Degree=2 IsPeriodic=0
    g143: GeomPoint X=179.022 Y=-85.8163 Z=0
    g144: GeomPoint X=171.895 Y=-91.7794 Z=0
    g145: Circle CenterX=185.124 CenterY=-86.2028 CenterZ=0 NormalX=0 NormalY=0 NormalZ=1 AngleXU=0 Radius=1
    g146: Circle CenterX=185.124 CenterY=-91.7794 CenterZ=0 NormalX=0 NormalY=0 NormalZ=1 AngleXU=0 Radius=1
    g147: Circle CenterX=191.747 CenterY=-91.7794 CenterZ=0 NormalX=0 NormalY=0 NormalZ=1 AngleXU=0 Radius=1
    g148: BSplineCurve PolesCount=3 KnotsCount=2 Degree=2 IsPeriodic=0
    g149: GeomPoint X=185.124 Y=-86.2028 Z=0
    g150: GeomPoint X=191.747 Y=-91.7794 Z=0
    g151: Circle CenterX=299.888 CenterY=-86.6413 CenterZ=0 NormalX=0 NormalY=0 NormalZ=1 AngleXU=0 Radius=1
    g152: Circle CenterX=306.073 CenterY=-91.7794 CenterZ=0 NormalX=0 NormalY=0 NormalZ=1 AngleXU=0 Radius=1
    g153: Circle CenterX=298.776 CenterY=-91.7794 CenterZ=0 NormalX=0 NormalY=0 NormalZ=1 AngleXU=0 Radius=1
    g154: BSplineCurve PolesCount=3 KnotsCount=2 Degree=2 IsPeriodic=0
    g155: GeomPoint X=299.888 Y=-86.6413 Z=0
    g156: GeomPoint X=298.776 Y=-91.7794 Z=0
    g157: LineSegment StartX=189.124 StartY=5.37834 StartZ=0 EndX=299.888 EndY=-86.6413 EndZ=0
    g158: LineSegment StartX=298.776 StartY=-91.7794 StartZ=0 EndX=191.747 EndY=-91.7794 EndZ=0
    g159: LineSegment StartX=185.124 StartY=-86.2028 StartZ=0 EndX=185.124 EndY=5.34704 EndZ=0
    g160: LineSegment StartX=179.022 StartY=5.34704 StartZ=0 EndX=179.022 EndY=-85.8163 EndZ=0
    g161: LineSegment StartX=171.895 StartY=-91.7794 StartZ=0 EndX=63.9135 EndY=-91.7794 EndZ=0
    g162: LineSegment StartX=61.6457 StartY=-88.8112 StartZ=0 EndX=175.022 EndY=5.37834 EndZ=0
    g163: Circle CenterX=302.073 CenterY=124.221 CenterZ=0 NormalX=0 NormalY=0 NormalZ=1 AngleXU=0 Radius=1
    g164: Circle CenterX=306.073 CenterY=124.221 CenterZ=0 NormalX=0 NormalY=0 NormalZ=1 AngleXU=0 Radius=1
    g165: Circle CenterX=302.996 CenterY=121.665 CenterZ=0 NormalX=0 NormalY=0 NormalZ=1 AngleXU=0 Radius=1
    g166: BSplineCurve PolesCount=3 KnotsCount=2 Degree=2 IsPeriodic=0
    g167: GeomPoint X=302.073 Y=124.221 Z=0
    g168: GeomPoint X=302.996 Y=121.665 Z=0
    g169: Circle CenterX=189.124 CenterY=124.221 CenterZ=0 NormalX=0 NormalY=0 NormalZ=1 AngleXU=0 Radius=1
    g170: Circle CenterX=185.124 CenterY=124.221 CenterZ=0 NormalX=0 NormalY=0 NormalZ=1 AngleXU=0 Radius=1
    g171: Circle CenterX=185.124 CenterY=120.221 CenterZ=0 NormalX=0 NormalY=0 NormalZ=1 AngleXU=0 Radius=1
    g172: BSplineCurve PolesCount=3 KnotsCount=2 Degree=2 IsPeriodic=0
    g173: GeomPoint X=189.124 Y=124.221 Z=0
    g174: GeomPoint X=185.124 Y=120.221 Z=0
    g175: Circle CenterX=175.022 CenterY=124.221 CenterZ=0 NormalX=0 NormalY=0 NormalZ=1 AngleXU=0 Radius=1
    g176: Circle CenterX=179.022 CenterY=124.221 CenterZ=0 NormalX=0 NormalY=0 NormalZ=1 AngleXU=0 Radius=1
    g177: Circle CenterX=179.022 CenterY=120.221 CenterZ=0 NormalX=0 NormalY=0 NormalZ=1 AngleXU=0 Radius=1
    g178: BSplineCurve PolesCount=3 KnotsCount=2 Degree=2 IsPeriodic=0
    g179: GeomPoint X=175.022 Y=124.221 Z=0
    g180: GeomPoint X=179.022 Y=120.221 Z=0
    g181: Circle CenterX=62.0728 CenterY=124.221 CenterZ=0 NormalX=0 NormalY=0 NormalZ=1 AngleXU=0 Radius=1
    g182: Circle CenterX=58.0728 CenterY=124.221 CenterZ=0 NormalX=0 NormalY=0 NormalZ=1 AngleXU=0 Radius=1
    g183: Circle CenterX=61.1496 CenterY=121.665 CenterZ=0 NormalX=0 NormalY=0 NormalZ=1 AngleXU=0 Radius=1
    g184: BSplineCurve PolesCount=3 KnotsCount=2 Degree=2 IsPeriodic=0
    g185: GeomPoint X=62.0728 Y=124.221 Z=0
    g186: GeomPoint X=61.1496 Y=121.665 Z=0
    g187: LineSegment StartX=62.0728 StartY=124.221 StartZ=0 EndX=175.022 EndY=124.221 EndZ=0
    g188: LineSegment StartX=179.022 StartY=120.221 StartZ=0 EndX=179.022 EndY=27.0628 EndZ=0
    g189: LineSegment StartX=185.124 StartY=27.0628 StartZ=0 EndX=185.124 EndY=120.221 EndZ=0
    g190: LineSegment StartX=189.124 StartY=124.221 StartZ=0 EndX=302.073 EndY=124.221 EndZ=0
    g191: LineSegment StartX=302.996 StartY=121.665 StartZ=0 EndX=189.124 EndY=27.0628 EndZ=0
    g192: LineSegment StartX=175.022 StartY=27.0628 StartZ=0 EndX=61.1496 EndY=121.665 EndZ=0
    g193: Circle CenterX=61.5791 CenterY=75.4095 CenterZ=0 NormalX=0 NormalY=0 NormalZ=1 AngleXU=0 Radius=1
    g194: Circle CenterX=58.0728 CenterY=77.3346 CenterZ=0 NormalX=0 NormalY=0 NormalZ=1 AngleXU=0 Radius=1
    g195: Circle CenterX=58.0728 CenterY=73.3346 CenterZ=0 NormalX=0 NormalY=0 NormalZ=1 AngleXU=0 Radius=1
    g196: BSplineCurve PolesCount=3 KnotsCount=2 Degree=2 IsPeriodic=0
    g197: GeomPoint X=61.5791 Y=75.4095 Z=0
    g198: GeomPoint X=58.0728 Y=73.3346 Z=0
    g199: Circle CenterX=58.0728 CenterY=-40.8935 CenterZ=0 NormalX=0 NormalY=0 NormalZ=1 AngleXU=0 Radius=1
    g200: Circle CenterX=58.0728 CenterY=-44.8935 CenterZ=0 NormalX=0 NormalY=0 NormalZ=1 AngleXU=0 Radius=1
    g201: Circle CenterX=61.5791 CenterY=-42.9683 CenterZ=0 NormalX=0 NormalY=0 NormalZ=1 AngleXU=0 Radius=1
    g202: BSplineCurve PolesCount=3 KnotsCount=2 Degree=2 IsPeriodic=0
    g203: GeomPoint X=58.0728 Y=-40.8935 Z=0
    g204: GeomPoint X=61.5791 Y=-42.9683 Z=0
    g205: LineSegment StartX=61.5791 StartY=-42.9683 StartZ=0 EndX=165.871 EndY=14.2954 EndZ=0
    g206: LineSegment StartX=165.871 StartY=18.1458 StartZ=0 EndX=61.5791 EndY=75.4095 EndZ=0
    g207: LineSegment StartX=58.0728 StartY=73.3346 StartZ=0 EndX=58.0728 EndY=-40.8935 EndZ=0
    g208: Circle CenterX=302.567 CenterY=-42.9683 CenterZ=0 NormalX=0 NormalY=0 NormalZ=1 AngleXU=0 Radius=1
    g209: Circle CenterX=306.073 CenterY=-44.8935 CenterZ=0 NormalX=0 NormalY=0 NormalZ=1 AngleXU=0 Radius=1
    g210: Circle CenterX=306.073 CenterY=-40.8935 CenterZ=0 NormalX=0 NormalY=0 NormalZ=1 AngleXU=0 Radius=1
    g211: BSplineCurve PolesCount=3 KnotsCount=2 Degree=2 IsPeriodic=0
    g212: GeomPoint X=302.567 Y=-42.9683 Z=0
    g213: GeomPoint X=306.073 Y=-40.8935 Z=0
    g214: Circle CenterX=306.073 CenterY=73.3346 CenterZ=0 NormalX=0 NormalY=0 NormalZ=1 AngleXU=0 Radius=1
    g215: Circle CenterX=306.073 CenterY=77.3346 CenterZ=0 NormalX=0 NormalY=0 NormalZ=1 AngleXU=0 Radius=1
    g216: Circle CenterX=302.567 CenterY=75.4095 CenterZ=0 NormalX=0 NormalY=0 NormalZ=1 AngleXU=0 Radius=1
    g217: BSplineCurve PolesCount=3 KnotsCount=2 Degree=2 IsPeriodic=0
    g218: GeomPoint X=306.073 Y=73.3346 Z=0
    g219: GeomPoint X=302.567 Y=75.4095 Z=0
    g220: LineSegment StartX=302.567 StartY=-42.9683 StartZ=0 EndX=198.275 EndY=14.2954 EndZ=0
    g221: LineSegment StartX=198.275 StartY=18.1458 StartZ=0 EndX=302.567 EndY=75.4095 EndZ=0
    g222: LineSegment StartX=306.073 StartY=73.3346 StartZ=0 EndX=306.073 EndY=-40.8935 EndZ=0
    g223: LineSegment StartX=322.073 StartY=105.865 StartZ=0 EndX=328.643 EndY=105.865 EndZ=0
    g224: LineSegment StartX=318.073 StartY=120.221 StartZ=0 EndX=318.073 EndY=109.865 EndZ=0
    g225: LineSegment StartX=336.157 StartY=107.779 StartZ=0 EndX=362.567 EndY=122.294 EndZ=0
    g226: Circle CenterX=362.073 CenterY=124.221 CenterZ=0 NormalX=0 NormalY=0 NormalZ=1 AngleXU=0 Radius=1
    g227: Circle CenterX=366.073 CenterY=124.221 CenterZ=0 NormalX=0 NormalY=0 NormalZ=1 AngleXU=0 Radius=1
    g228: Circle CenterX=362.567 CenterY=122.294 CenterZ=0 NormalX=0 NormalY=0 NormalZ=1 AngleXU=0 Radius=1
    g229: BSplineCurve PolesCount=3 KnotsCount=2 Degree=2 IsPeriodic=0
    g230: GeomPoint X=362.073 Y=124.221 Z=0
    g231: GeomPoint X=362.567 Y=122.294 Z=0
    g232: Circle CenterX=322.073 CenterY=124.221 CenterZ=0 NormalX=0 NormalY=0 NormalZ=1 AngleXU=0 Radius=1
    g233: Circle CenterX=318.073 CenterY=124.221 CenterZ=0 NormalX=0 NormalY=0 NormalZ=1 AngleXU=0 Radius=1
    g234: Circle CenterX=318.073 CenterY=120.221 CenterZ=0 NormalX=0 NormalY=0 NormalZ=1 AngleXU=0 Radius=1
    g235: BSplineCurve PolesCount=3 KnotsCount=2 Degree=2 IsPeriodic=0
    g236: GeomPoint X=322.073 Y=124.221 Z=0
    g237: GeomPoint X=318.073 Y=120.221 Z=0
    g238: Circle CenterX=322.073 CenterY=105.865 CenterZ=0 NormalX=0 NormalY=0 NormalZ=1 AngleXU=0 Radius=1
    g239: Circle CenterX=318.073 CenterY=105.865 CenterZ=0 NormalX=0 NormalY=0 NormalZ=1 AngleXU=0 Radius=1
    g240: Circle CenterX=318.073 CenterY=109.865 CenterZ=0 NormalX=0 NormalY=0 NormalZ=1 AngleXU=0 Radius=1
    g241: BSplineCurve PolesCount=3 KnotsCount=2 Degree=2 IsPeriodic=0
    g242: GeomPoint X=322.073 Y=105.865 Z=0
    g243: GeomPoint X=318.073 Y=109.865 Z=0
    g244: Circle CenterX=336.157 CenterY=107.779 CenterZ=0 NormalX=0 NormalY=0 NormalZ=1 AngleXU=0 Radius=1
    g245: Circle CenterX=332.651 CenterY=105.853 CenterZ=0 NormalX=0 NormalY=0 NormalZ=1 AngleXU=0 Radius=1
    g246: Circle CenterX=328.643 CenterY=105.865 CenterZ=0 NormalX=0 NormalY=0 NormalZ=1 AngleXU=0 Radius=1
    g247: BSplineCurve PolesCount=3 KnotsCount=2 Degree=2 IsPeriodic=0
    g248: GeomPoint X=336.157 Y=107.779 Z=0
    g249: GeomPoint X=328.643 Y=105.865 Z=0
    g250: LineSegment StartX=322.073 StartY=124.221 StartZ=0 EndX=362.073 EndY=124.221 EndZ=0
    g251: Circle CenterX=371.567 CenterY=-80.8644 CenterZ=0 NormalX=0 NormalY=0 NormalZ=1 AngleXU=0 Radius=1
    g252: Circle CenterX=375.073 CenterY=-82.7896 CenterZ=0 NormalX=0 NormalY=0 NormalZ=1 AngleXU=0 Radius=1
    g253: Circle CenterX=375.073 CenterY=-78.7896 CenterZ=0 NormalX=0 NormalY=0 NormalZ=1 AngleXU=0 Radius=1
    g254: BSplineCurve PolesCount=3 KnotsCount=2 Degree=2 IsPeriodic=0
    g255: GeomPoint X=371.567 Y=-80.8644 Z=0
    g256: GeomPoint X=375.073 Y=-78.7896 Z=0
    g257: Circle CenterX=321.579 CenterY=-53.4075 CenterZ=0 NormalX=0 NormalY=0 NormalZ=1 AngleXU=0 Radius=1
    g258: Circle CenterX=318.073 CenterY=-51.4823 CenterZ=0 NormalX=0 NormalY=0 NormalZ=1 AngleXU=0 Radius=1
    g259: Circle CenterX=318.073 CenterY=-47.4805 CenterZ=0 NormalX=0 NormalY=0 NormalZ=1 AngleXU=0 Radius=1
    g260: BSplineCurve PolesCount=3 KnotsCount=2 Degree=2 IsPeriodic=0
    g261: GeomPoint X=321.579 Y=-53.4075 Z=0
    g262: GeomPoint X=318.073 Y=-47.4805 Z=0
    g263: LineSegment StartX=371.567 StartY=-80.8644 StartZ=0 EndX=321.579 EndY=-53.4075 EndZ=0
    g264: Circle CenterX=321.579 CenterY=-67.3492 CenterZ=0 NormalX=0 NormalY=0 NormalZ=1 AngleXU=0 Radius=1
    g265: Circle CenterX=318.073 CenterY=-65.424 CenterZ=0 NormalX=0 NormalY=0 NormalZ=1 AngleXU=0 Radius=1
    g266: Circle CenterX=318.073 CenterY=-69.424 CenterZ=0 NormalX=0 NormalY=0 NormalZ=1 AngleXU=0 Radius=1
    g267: BSplineCurve PolesCount=3 KnotsCount=2 Degree=2 IsPeriodic=0
    g268: GeomPoint X=321.579 Y=-67.3492 Z=0
    g269: GeomPoint X=318.073 Y=-69.424 Z=0
    g270: Circle CenterX=362.567 CenterY=-89.8542 CenterZ=0 NormalX=0 NormalY=0 NormalZ=1 AngleXU=0 Radius=1
    g271: Circle CenterX=366.073 CenterY=-91.7794 CenterZ=0 NormalX=0 NormalY=0 NormalZ=1 AngleXU=0 Radius=1
    g272: Circle CenterX=362.073 CenterY=-91.7794 CenterZ=0 NormalX=0 NormalY=0 NormalZ=1 AngleXU=0 Radius=1
    g273: BSplineCurve PolesCount=3 KnotsCount=2 Degree=2 IsPeriodic=0
    g274: GeomPoint X=362.567 Y=-89.8542 Z=0
    g275: GeomPoint X=362.073 Y=-91.7794 Z=0
    g276: Circle CenterX=322.073 CenterY=-91.7794 CenterZ=0 NormalX=0 NormalY=0 NormalZ=1 AngleXU=0 Radius=1
    g277: Circle CenterX=318.073 CenterY=-91.7794 CenterZ=0 NormalX=0 NormalY=0 NormalZ=1 AngleXU=0 Radius=1
    g278: Circle CenterX=318.073 CenterY=-87.7794 CenterZ=0 NormalX=0 NormalY=0 NormalZ=1 AngleXU=0 Radius=1
    g279: BSplineCurve PolesCount=3 KnotsCount=2 Degree=2 IsPeriodic=0
    g280: GeomPoint X=322.073 Y=-91.7794 Z=0
    g281: GeomPoint X=318.073 Y=-87.7794 Z=0
    g282: LineSegment StartX=362.567 StartY=-89.8542 StartZ=0 EndX=321.579 EndY=-67.3492 EndZ=0
    g283: LineSegment StartX=318.073 StartY=-69.424 StartZ=0 EndX=318.073 EndY=-87.7794 EndZ=0
    g284: LineSegment StartX=322.073 StartY=-91.7794 StartZ=0 EndX=362.073 EndY=-91.7794 EndZ=0
    g285: Circle CenterX=2.07281 CenterY=124.221 CenterZ=0 NormalX=0 NormalY=0 NormalZ=1 AngleXU=0 Radius=1
    g286: Circle CenterX=1.57905 CenterY=122.295 CenterZ=0 NormalX=0 NormalY=0 NormalZ=1 AngleXU=0 Radius=1
    g287: BSplineCurve PolesCount=3 KnotsCount=2 Degree=2 IsPeriodic=0
    g288: GeomPoint X=2.07281 Y=124.221 Z=0
    g289: GeomPoint X=1.57905 Y=122.295 Z=0
    g290: Circle CenterX=42.0728 CenterY=124.221 CenterZ=0 NormalX=0 NormalY=0 NormalZ=1 AngleXU=0 Radius=1
    g291: Circle CenterX=46.0728 CenterY=124.221 CenterZ=0 NormalX=0 NormalY=0 NormalZ=1 AngleXU=0 Radius=1
    g292: Circle CenterX=46.0728 CenterY=120.221 CenterZ=0 NormalX=0 NormalY=0 NormalZ=1 AngleXU=0 Radius=1
    g293: BSplineCurve PolesCount=3 KnotsCount=2 Degree=2 IsPeriodic=0
    g294: GeomPoint X=42.0728 Y=124.221 Z=0
    g295: GeomPoint X=46.0728 Y=120.221 Z=0
    g296: Circle CenterX=46.0728 CenterY=109.865 CenterZ=0 NormalX=0 NormalY=0 NormalZ=1 AngleXU=0 Radius=1
    g297: Circle CenterX=46.0728 CenterY=105.865 CenterZ=0 NormalX=0 NormalY=0 NormalZ=1 AngleXU=0 Radius=1
    g298: Circle CenterX=42.0728 CenterY=105.865 CenterZ=0 NormalX=0 NormalY=0 NormalZ=1 AngleXU=0 Radius=1
    g299: BSplineCurve PolesCount=3 KnotsCount=2 Degree=2 IsPeriodic=0
    g300: GeomPoint X=46.0728 Y=109.865 Z=0
    g301: GeomPoint X=42.0728 Y=105.865 Z=0
    g302: Circle CenterX=35.5028 CenterY=105.865 CenterZ=0 NormalX=0 NormalY=0 NormalZ=1 AngleXU=0 Radius=1
    g303: Circle CenterX=31.5028 CenterY=105.865 CenterZ=0 NormalX=0 NormalY=0 NormalZ=1 AngleXU=0 Radius=1
    g304: Circle CenterX=27.9965 CenterY=107.79 CenterZ=0 NormalX=0 NormalY=0 NormalZ=1 AngleXU=0 Radius=1
    g305: BSplineCurve PolesCount=3 KnotsCount=2 Degree=2 IsPeriodic=0
    g306: GeomPoint X=35.5028 Y=105.865 Z=0
    g307: GeomPoint X=27.9965 Y=107.79 Z=0
    g308: LineSegment StartX=2.07281 StartY=124.221 StartZ=0 EndX=42.0728 EndY=124.221 EndZ=0
    g309: LineSegment StartX=46.0728 StartY=120.221 StartZ=0 EndX=46.0728 EndY=109.865 EndZ=0
    g310: LineSegment StartX=42.0728 StartY=105.865 StartZ=0 EndX=35.5028 EndY=105.865 EndZ=0
    g311: LineSegment StartX=27.9965 StartY=107.79 StartZ=0 EndX=1.57905 EndY=122.295 EndZ=0
    g312: Circle CenterX=42.5666 CenterY=-67.3492 CenterZ=0 NormalX=0 NormalY=0 NormalZ=1 AngleXU=0 Radius=1
    g313: Circle CenterX=46.0728 CenterY=-65.424 CenterZ=0 NormalX=0 NormalY=0 NormalZ=1 AngleXU=0 Radius=1
    g314: Circle CenterX=46.0728 CenterY=-69.424 CenterZ=0 NormalX=0 NormalY=0 NormalZ=1 AngleXU=0 Radius=1
    g315: BSplineCurve PolesCount=3 KnotsCount=2 Degree=2 IsPeriodic=0
    g316: GeomPoint X=42.5666 Y=-67.3492 Z=0
    g317: GeomPoint X=46.0728 Y=-69.424 Z=0
    g318: Circle CenterX=46.0728 CenterY=-87.7794 CenterZ=0 NormalX=0 NormalY=0 NormalZ=1 AngleXU=0 Radius=1
    g319: Circle CenterX=46.0728 CenterY=-91.7794 CenterZ=0 NormalX=0 NormalY=0 NormalZ=1 AngleXU=0 Radius=1
    g320: Circle CenterX=42.0728 CenterY=-91.7794 CenterZ=0 NormalX=0 NormalY=0 NormalZ=1 AngleXU=0 Radius=1
    g321: BSplineCurve PolesCount=3 KnotsCount=2 Degree=2 IsPeriodic=0
    g322: GeomPoint X=46.0728 Y=-87.7794 Z=0
    g323: GeomPoint X=42.0728 Y=-91.7794 Z=0
    g324: Circle CenterX=2.07281 CenterY=-91.7794 CenterZ=0 NormalX=0 NormalY=0 NormalZ=1 AngleXU=0 Radius=1
    g325: Circle CenterX=-1.92719 CenterY=-91.7794 CenterZ=0 NormalX=0 NormalY=0 NormalZ=1 AngleXU=0 Radius=1
    g326: Circle CenterX=1.57905 CenterY=-89.8542 CenterZ=0 NormalX=0 NormalY=0 NormalZ=1 AngleXU=0 Radius=1
    g327: BSplineCurve PolesCount=3 KnotsCount=2 Degree=2 IsPeriodic=0
    g328: GeomPoint X=2.07281 Y=-91.7794 Z=0
    g329: GeomPoint X=1.57905 Y=-89.8542 Z=0
    g330: LineSegment StartX=2.07281 StartY=-91.7794 StartZ=0 EndX=42.0728 EndY=-91.7794 EndZ=0
    g331: LineSegment StartX=46.0728 StartY=-87.7794 StartZ=0 EndX=46.0728 EndY=-69.424 EndZ=0
    g332: LineSegment StartX=42.5666 StartY=-67.3492 StartZ=0 EndX=1.57905 EndY=-89.8542 EndZ=0
    g333: Circle CenterX=322.073 CenterY=76.4095 CenterZ=0 NormalX=0 NormalY=0 NormalZ=1 AngleXU=0 Radius=4
    g334: BSplineCurve PolesCount=3 KnotsCount=2 Degree=2 IsPeriodic=0
    g335: GeomPoint X=318.073 Y=72.4095 Z=0
    g336: GeomPoint X=322.073 Y=76.4095 Z=0
    g337: Circle CenterX=375.073 CenterY=72.4095 CenterZ=0 NormalX=0 NormalY=0 NormalZ=1 AngleXU=0 Radius=1
    g338: Circle CenterX=375.073 CenterY=76.4095 CenterZ=0 NormalX=0 NormalY=0 NormalZ=1 AngleXU=0 Radius=1
    g339: Circle CenterX=371.073 CenterY=76.4095 CenterZ=0 NormalX=0 NormalY=0 NormalZ=1 AngleXU=0 Radius=1
    g340: BSplineCurve PolesCount=3 KnotsCount=2 Degree=2 IsPeriodic=0
    g341: GeomPoint X=375.073 Y=72.4095 Z=0
    g342: GeomPoint X=371.073 Y=76.4095 Z=0
    g343: LineSegment StartX=322.073 StartY=76.4095 StartZ=0 EndX=371.073 EndY=76.4095 EndZ=0
    g344: LineSegment StartX=318.073 StartY=72.4095 StartZ=0 EndX=318.073 EndY=-47.4805 EndZ=0
    g345: LineSegment StartX=375.073 StartY=72.4095 StartZ=0 EndX=375.073 EndY=-78.7896 EndZ=0
    g346: ArcOfCircle CenterX=-26.9272 CenterY=22.1087 CenterZ=0 NormalX=0 NormalY=0 NormalZ=1 AngleXU=0 Radius=4 StartAngle=5e-16 EndAngle=3.14159
    g347: LineSegment StartX=-22.9272 StartY=22.1087 StartZ=0 EndX=-18.9272 EndY=-83.7794 EndZ=0
    g348: LineSegment StartX=-34.9272 StartY=-83.7794 StartZ=0 EndX=-30.9272 EndY=22.1087 EndZ=0
    g349: LineSegment StartX=383.073 StartY=22.1087 StartZ=0 EndX=386.483 EndY=22.1087 EndZ=0
    g350: LineSegment StartX=399.073 StartY=22.1087 StartZ=0 EndX=394.711 EndY=22.1087 EndZ=0
  constraints (576):
    c: Coincident(g0,g2)
    c: Block(g0)
    c: Block(g1)
    c: Vertical(g3)
    c: Vertical(g4)
    c: Block(g4)
    c: Block(g3)
    c: Tangent(g6,g7) = 1.5708
    c: Tangent(g7,g9) = 1.5708
    c: Equal(g6,g9)
    c: Coincident(g8,g6)
    c: Coincident(g8,g9)
    c: Block(g7)
    c: Block(g8)
    c: Weight(g10) = 1
    c: Equal(g10,g11)
    c: Equal(g10,g12)
    c: InternalAlignment(g10,g13)
    c: InternalAlignment(g11,g13)
    c: InternalAlignment(g12,g13)
    c: InternalAlignment(g14,g13)
    c: InternalAlignment(g15,g13)
    c: Weight(g16) = 1
    c: Equal(g16,g17)
    c: Equal(g16,g18)
    c: InternalAlignment(g16,g19)
    c: InternalAlignment(g17,g19)
    c: InternalAlignment(g18,g19)
    c: InternalAlignment(g20,g19)
    c: InternalAlignment(g21,g19)
    c: Block(g19)
    c: Block(g13)
    c: Weight(g22) = 1
    c: Equal(g22,g23)
    c: Equal(g22,g24)
    c: InternalAlignment(g22,g25)
    c: InternalAlignment(g23,g25)
    c: InternalAlignment(g24,g25)
    c: InternalAlignment(g26,g25)
    c: InternalAlignment(g27,g25)
    c: Weight(g28) = 1
    c: Equal(g28,g29)
    c: Equal(g28,g30)
    c: InternalAlignment(g28,g31)
    c: InternalAlignment(g29,g31)
    c: InternalAlignment(g30,g31)
    c: InternalAlignment(g32,g31)
    c: InternalAlignment(g33,g31)
    c: Block(g31)
    c: Block(g25)
    c: Weight(g34) = 1
    c: Equal(g34,g35)
    c: Equal(g34,g36)
    c: InternalAlignment(g34,g37)
    c: InternalAlignment(g35,g37)
    c: InternalAlignment(g36,g37)
    c: InternalAlignment(g38,g37)
    c: InternalAlignment(g39,g37)
    c: Weight(g40) = 1
    c: Equal(g40,g41)
    c: Equal(g40,g42)
    c: InternalAlignment(g40,g43)
    c: InternalAlignment(g41,g43)
    c: InternalAlignment(g42,g43)
    c: InternalAlignment(g44,g43)
    c: InternalAlignment(g45,g43)
    c: Block(g37)
    c: Block(g43)
    c: Coincident(g46,g4)
    c: Coincident(g46,g3)
    c: Horizontal(g46)
    c: Distance(g46) = 450
    c: Coincident(g47,g4)
    c: Coincident(g47,g3)
    c: Horizontal(g47)
    c: Horizontal(g48)
    c: Coincident(g2,g48)
    c: Block(g48)
    c: Coincident(g1,g48)
    c: Weight(g49) = 1
    c: Equal(g49,g50)
    c: Equal(g49,g51)
    c: InternalAlignment(g49,g52)
    c: InternalAlignment(g50,g52)
    c: InternalAlignment(g51,g52)
    c: InternalAlignment(g53,g52)
    c: InternalAlignment(g54,g52)
    c: Block(g52)
    c: Weight(g55) = 1
    c: Equal(g55,g56)
    c: Equal(g55,g57)
    c: InternalAlignment(g55,g58)
    c: InternalAlignment(g56,g58)
    c: InternalAlignment(g57,g58)
    c: InternalAlignment(g59,g58)
    c: InternalAlignment(g60,g58)
    c: Block(g58)
    c: Weight(g61) = 1
    c: Equal(g61,g62)
    c: Equal(g61,g63)
    c: InternalAlignment(g61,g64)
    c: InternalAlignment(g62,g64)
    c: InternalAlignment(g63,g64)
    c: InternalAlignment(g65,g64)
    c: InternalAlignment(g66,g64)
    c: Block(g64)
    c: Weight(g67) = 1
    c: Equal(g67,g68)
    c: Equal(g67,g69)
    c: InternalAlignment(g67,g70)
    c: InternalAlignment(g68,g70)
    c: InternalAlignment(g69,g70)
    c: InternalAlignment(g71,g70)
    c: InternalAlignment(g72,g70)
    c: Block(g70)
    c: Weight(g73) = 1
    c: Equal(g73,g74)
    c: Equal(g73,g75)
    c: InternalAlignment(g73,g76)
    c: InternalAlignment(g74,g76)
    c: InternalAlignment(g75,g76)
    c: InternalAlignment(g77,g76)
    c: InternalAlignment(g78,g76)
    c: Weight(g79) = 1
    c: Equal(g79,g80)
    c: Equal(g79,g81)
    c: InternalAlignment(g79,g82)
    c: InternalAlignment(g80,g82)
    c: InternalAlignment(g81,g82)
    c: InternalAlignment(g83,g82)
    c: InternalAlignment(g84,g82)
    c: Block(g76)
    c: Block(g82)
    c: Coincident(g85,g76)
    c: Coincident(g85,g82)
    c: Vertical(g85)
    c: Coincident(g86,g76)
    c: Coincident(g86,g58)
    c: Coincident(g87,g58)
    c: Coincident(g87,g82)
    c: Weight(g88) = 1
    c: Equal(g88,g89)
    c: Equal(g88,g90)
    c: InternalAlignment(g88,g91)
    c: InternalAlignment(g89,g91)
    c: InternalAlignment(g90,g91)
    c: InternalAlignment(g92,g91)
    c: InternalAlignment(g93,g91)
    c: Weight(g94) = 1
    c: Equal(g94,g95)
    c: Equal(g94,g96)
    c: InternalAlignment(g94,g97)
    c: InternalAlignment(g95,g97)
    c: InternalAlignment(g96,g97)
    c: InternalAlignment(g98,g97)
    c: InternalAlignment(g99,g97)
    c: Block(g91)
    c: Block(g97)
    c: Coincident(g100,g91)
    c: Coincident(g100,g97)
    c: Vertical(g100)
    c: Coincident(g101,g91)
    c: Coincident(g101,g52)
    c: Coincident(g102,g52)
    c: Coincident(g102,g97)
    c: Weight(g103) = 1
    c: Equal(g103,g104)
    c: Equal(g103,g105)
    c: InternalAlignment(g103,g106)
    c: InternalAlignment(g104,g106)
    c: InternalAlignment(g105,g106)
    c: InternalAlignment(g107,g106)
    c: InternalAlignment(g108,g106)
    c: Weight(g109) = 1
    c: Equal(g109,g110)
    c: Equal(g109,g111)
    c: InternalAlignment(g109,g112)
    c: InternalAlignment(g110,g112)
    c: InternalAlignment(g111,g112)
    c: InternalAlignment(g113,g112)
    c: InternalAlignment(g114,g112)
    c: Block(g106)
    c: Block(g112)
    c: Coincident(g115,g106)
    c: Coincident(g115,g112)
    c: Vertical(g115)
    c: Coincident(g116,g112)
    c: Coincident(g116,g70)
    c: Coincident(g117,g70)
    c: Coincident(g117,g106)
    c: Weight(g118) = 1
    c: Equal(g118,g119)
    c: Equal(g118,g120)
    c: InternalAlignment(g118,g121)
    c: InternalAlignment(g119,g121)
    c: InternalAlignment(g120,g121)
    c: InternalAlignment(g122,g121)
    c: InternalAlignment(g123,g121)
    c: Weight(g124) = 1
    c: Equal(g124,g125)
    c: Equal(g124,g126)
    c: InternalAlignment(g124,g127)
    c: InternalAlignment(g125,g127)
    c: InternalAlignment(g126,g127)
    c: InternalAlignment(g128,g127)
    c: InternalAlignment(g129,g127)
    c: Block(g121)
    c: Block(g127)
    c: Coincident(g130,g121)
    c: Coincident(g130,g127)
    c: Vertical(g130)
    c: Coincident(g131,g127)
    c: Coincident(g131,g64)
    c: Coincident(g132,g64)
    c: Coincident(g132,g121)
    c: Weight(g133) = 1
    c: Equal(g133,g134)
    c: Equal(g133,g135)
    c: InternalAlignment(g133,g136)
    c: InternalAlignment(g134,g136)
    c: InternalAlignment(g135,g136)
    c: InternalAlignment(g137,g136)
    c: InternalAlignment(g138,g136)
    c: Weight(g139) = 1
    c: Equal(g139,g140)
    c: Equal(g139,g141)
    c: InternalAlignment(g139,g142)
    c: InternalAlignment(g140,g142)
    c: InternalAlignment(g141,g142)
    c: InternalAlignment(g143,g142)
    c: InternalAlignment(g144,g142)
    c: Weight(g145) = 1
    c: Equal(g145,g146)
    c: Equal(g145,g147)
    c: InternalAlignment(g145,g148)
    c: InternalAlignment(g146,g148)
    c: InternalAlignment(g147,g148)
    c: InternalAlignment(g149,g148)
    c: InternalAlignment(g150,g148)
    c: Weight(g151) = 1
    c: Equal(g151,g152)
    c: Equal(g151,g153)
    c: InternalAlignment(g151,g154)
    c: InternalAlignment(g152,g154)
    c: InternalAlignment(g153,g154)
    c: InternalAlignment(g155,g154)
    c: InternalAlignment(g156,g154)
    c: Block(g154)
    c: Block(g148)
    c: Block(g142)
    c: Block(g136)
    c: Coincident(g157,g31)
    c: Coincident(g157,g154)
    c: Coincident(g158,g154)
    c: Coincident(g158,g148)
    c: Horizontal(g158)
    c: Coincident(g159,g148)
    c: Coincident(g159,g31)
    c: Vertical(g159)
    c: Coincident(g160,g25)
    c: Coincident(g160,g142)
    c: Vertical(g160)
    c: Coincident(g161,g142)
    c: Coincident(g161,g136)
    c: Horizontal(g161)
    c: Coincident(g162,g136)
    c: Coincident(g162,g25)
    c: Weight(g163) = 1
    c: Equal(g163,g164)
    c: Equal(g163,g165)
    c: InternalAlignment(g163,g166)
    c: InternalAlignment(g164,g166)
    c: InternalAlignment(g165,g166)
    c: InternalAlignment(g167,g166)
    c: InternalAlignment(g168,g166)
    c: Weight(g169) = 1
    c: Equal(g169,g170)
    c: Equal(g169,g171)
    c: InternalAlignment(g169,g172)
    c: InternalAlignment(g170,g172)
    c: InternalAlignment(g171,g172)
    c: InternalAlignment(g173,g172)
    c: InternalAlignment(g174,g172)
    c: Weight(g175) = 1
    c: Equal(g175,g176)
    c: Equal(g175,g177)
    c: InternalAlignment(g175,g178)
    c: InternalAlignment(g176,g178)
    c: InternalAlignment(g177,g178)
    c: InternalAlignment(g179,g178)
    c: InternalAlignment(g180,g178)
    c: Weight(g181) = 1
    c: Equal(g181,g182)
    c: Equal(g181,g183)
    c: InternalAlignment(g181,g184)
    c: InternalAlignment(g182,g184)
    c: InternalAlignment(g183,g184)
    c: InternalAlignment(g185,g184)
    c: InternalAlignment(g186,g184)
    c: Block(g184)
    c: Block(g178)
    c: Block(g172)
    c: Block(g166)
    c: Coincident(g187,g184)
    c: Coincident(g187,g178)
    c: Horizontal(g187)
    c: Coincident(g188,g178)
    c: Coincident(g188,g13)
    c: Vertical(g188)
    c: Coincident(g189,g19)
    c: Coincident(g189,g172)
    c: Vertical(g189)
    c: Coincident(g190,g172)
    c: Coincident(g190,g166)
    c: Horizontal(g190)
    c: Coincident(g191,g166)
    c: Coincident(g191,g19)
    c: Coincident(g192,g13)
    c: Weight(g193) = 1
    c: Equal(g193,g194)
    c: Equal(g193,g195)
    c: InternalAlignment(g193,g196)
    c: InternalAlignment(g194,g196)
    c: InternalAlignment(g195,g196)
    c: InternalAlignment(g197,g196)
    c: InternalAlignment(g198,g196)
    c: Weight(g199) = 1
    c: Equal(g199,g200)
    c: Equal(g199,g201)
    c: InternalAlignment(g199,g202)
    c: InternalAlignment(g200,g202)
    c: InternalAlignment(g201,g202)
    c: InternalAlignment(g203,g202)
    c: InternalAlignment(g204,g202)
    c: Block(g202)
    c: Block(g196)
    c: Coincident(g205,g202)
    c: Coincident(g205,g37)
    c: Coincident(g206,g37)
    c: Coincident(g206,g196)
    c: Coincident(g207,g196)
    c: Coincident(g207,g202)
    c: Vertical(g207)
    c: Weight(g208) = 1
    c: Equal(g208,g209)
    c: Equal(g208,g210)
    c: InternalAlignment(g208,g211)
    c: InternalAlignment(g209,g211)
    c: InternalAlignment(g210,g211)
    c: InternalAlignment(g212,g211)
    c: InternalAlignment(g213,g211)
    c: Weight(g214) = 1
    c: Equal(g214,g215)
    c: Equal(g214,g216)
    c: InternalAlignment(g214,g217)
    c: InternalAlignment(g215,g217)
    c: InternalAlignment(g216,g217)
    c: InternalAlignment(g218,g217)
    c: InternalAlignment(g219,g217)
    c: Block(g217)
    c: Block(g211)
    c: Coincident(g220,g211)
    c: Coincident(g220,g43)
    c: Coincident(g221,g43)
    c: Coincident(g221,g217)
    c: Coincident(g222,g217)
    c: Coincident(g222,g211)
    c: Vertical(g222)
    c: Horizontal(g223)
    c: Block(g223)
    c: Vertical(g224)
    c: Block(g224)
    c: Block(g225)
    c: Weight(g226) = 1
    c: Equal(g226,g227)
    c: Equal(g226,g228)
    c: InternalAlignment(g226,g229)
    c: InternalAlignment(g227,g229)
    c: InternalAlignment(g228,g229)
    c: InternalAlignment(g230,g229)
    c: InternalAlignment(g231,g229)
    c: Weight(g232) = 1
    c: Equal(g232,g233)
    c: Equal(g232,g234)
    c: InternalAlignment(g232,g235)
    c: InternalAlignment(g233,g235)
    c: InternalAlignment(g234,g235)
    c: InternalAlignment(g236,g235)
    c: InternalAlignment(g237,g235)
    c: Weight(g238) = 1
    c: Equal(g238,g239)
    c: Equal(g238,g240)
    c: InternalAlignment(g238,g241)
    c: InternalAlignment(g239,g241)
    c: InternalAlignment(g240,g241)
    c: InternalAlignment(g242,g241)
    c: InternalAlignment(g243,g241)
    c: Weight(g244) = 1
    c: Equal(g244,g245)
    c: Equal(g244,g246)
    c: InternalAlignment(g244,g247)
    c: InternalAlignment(g245,g247)
    c: InternalAlignment(g246,g247)
    c: InternalAlignment(g248,g247)
    c: InternalAlignment(g249,g247)
    c: Block(g229)
    c: Block(g235)
    c: Block(g241)
    c: Block(g247)
    c: Coincident(g250,g235)
    c: Coincident(g250,g229)
    c: Horizontal(g250)
    c: Block(g192)
    c: Weight(g251) = 1
    c: Equal(g251,g252)
    c: Equal(g251,g253)
    c: InternalAlignment(g251,g254)
    c: InternalAlignment(g252,g254)
    c: InternalAlignment(g253,g254)
    c: InternalAlignment(g255,g254)
    c: InternalAlignment(g256,g254)
    c: Weight(g257) = 1
    c: Equal(g257,g258)
    c: Equal(g257,g259)
    c: InternalAlignment(g257,g260)
    c: InternalAlignment(g258,g260)
    c: InternalAlignment(g259,g260)
    c: InternalAlignment(g261,g260)
    c: InternalAlignment(g262,g260)
    c: Block(g254)
    c: Block(g260)
    c: Coincident(g263,g254)
    c: Coincident(g263,g260)
    c: Weight(g264) = 1
    c: Equal(g264,g265)
    c: Equal(g264,g266)
    c: InternalAlignment(g264,g267)
    c: InternalAlignment(g265,g267)
    c: InternalAlignment(g266,g267)
    c: InternalAlignment(g268,g267)
    c: InternalAlignment(g269,g267)
    c: Weight(g270) = 1
    c: Equal(g270,g271)
    c: Equal(g270,g272)
    c: InternalAlignment(g270,g273)
    c: InternalAlignment(g271,g273)
    c: InternalAlignment(g272,g273)
    c: InternalAlignment(g274,g273)
    c: InternalAlignment(g275,g273)
    c: Weight(g276) = 1
    c: Equal(g276,g277)
    c: Equal(g276,g278)
    c: InternalAlignment(g276,g279)
    c: InternalAlignment(g277,g279)
    c: InternalAlignment(g278,g279)
    c: InternalAlignment(g280,g279)
    c: InternalAlignment(g281,g279)
    c: Block(g279)
    c: Block(g273)
    c: Block(g267)
    c: Coincident(g282,g273)
    c: Coincident(g282,g267)
    c: Coincident(g283,g267)
    c: Coincident(g283,g279)
    c: Vertical(g283)
    c: Coincident(g284,g279)
    c: Coincident(g284,g273)
    c: Horizontal(g284)
    c: Weight(g285) = 1
    c: Equal(g285,g286)
    c: InternalAlignment(g285,g287)
    c: InternalAlignment(g286,g287)
    c: InternalAlignment(g288,g287)
    c: InternalAlignment(g289,g287)
    c: Weight(g290) = 1
    c: InternalAlignment(g291,g293)
    c: InternalAlignment(g292,g293)
    c: InternalAlignment(g294,g293)
    c: InternalAlignment(g295,g293)
    c: Weight(g296) = 1
    c: Equal(g296,g297)
    c: Equal(g296,g298)
    c: InternalAlignment(g296,g299)
    c: InternalAlignment(g297,g299)
    c: InternalAlignment(g298,g299)
    c: InternalAlignment(g300,g299)
    c: InternalAlignment(g301,g299)
    c: Equal(g302,g303)
    c: Equal(g302,g304)
    c: InternalAlignment(g302,g305)
    c: InternalAlignment(g303,g305)
    c: InternalAlignment(g304,g305)
    c: InternalAlignment(g306,g305)
    c: InternalAlignment(g307,g305)
    c: Block(g293)
    c: Block(g299)
    c: Block(g305)
    c: Block(g287)
    c: Coincident(g308,g287)
    c: Coincident(g308,g293)
    c: Horizontal(g308)
    c: Coincident(g309,g293)
    c: Coincident(g309,g299)
    c: Vertical(g309)
    c: Coincident(g310,g299)
    c: Coincident(g310,g305)
    c: Horizontal(g310)
    c: Coincident(g311,g305)
    c: Coincident(g311,g287)
    c: Weight(g312) = 1
    c: Equal(g312,g313)
    c: Equal(g312,g314)
    c: InternalAlignment(g312,g315)
    c: InternalAlignment(g313,g315)
    c: InternalAlignment(g314,g315)
    c: InternalAlignment(g316,g315)
    c: InternalAlignment(g317,g315)
    c: Weight(g318) = 1
    c: Equal(g318,g319)
    c: Equal(g318,g320)
    c: InternalAlignment(g318,g321)
    c: InternalAlignment(g319,g321)
    c: InternalAlignment(g320,g321)
    c: InternalAlignment(g322,g321)
    c: InternalAlignment(g323,g321)
    c: Weight(g324) = 1
    c: Equal(g324,g325)
    c: Equal(g324,g326)
    c: InternalAlignment(g324,g327)
    c: InternalAlignment(g325,g327)
    c: InternalAlignment(g326,g327)
    c: InternalAlignment(g328,g327)
    c: InternalAlignment(g329,g327)
    c: Block(g327)
    c: Block(g321)
    c: Block(g315)
    c: Coincident(g330,g327)
    c: Coincident(g330,g321)
    c: Horizontal(g330)
    c: Coincident(g331,g321)
    c: Coincident(g331,g315)
    c: Vertical(g331)
    c: Coincident(g332,g315)
    c: Coincident(g332,g327)
    c: InternalAlignment(g333,g334)
    c: InternalAlignment(g335,g334)
    c: InternalAlignment(g336,g334)
    c: Block(g334)
    c: Equal(g337,g338)
    c: Equal(g337,g339)
    c: InternalAlignment(g337,g340)
    c: InternalAlignment(g338,g340)
    c: InternalAlignment(g339,g340)
    c: InternalAlignment(g341,g340)
    c: InternalAlignment(g342,g340)
    c: Block(g340)
    c: Coincident(g343,g334)
    c: Horizontal(g343)
    c: Block(g343)
    c: Coincident(g344,g334)
    c: Coincident(g344,g260)
    c: Vertical(g344)
    c: Coincident(g345,g340)
    c: Coincident(g345,g254)
    c: Vertical(g345)
    c: Block(g346)
    c: Block(g5)
    c: Distance(g344) = 119.89
    c: Coincident(g347,g346)
    c: Coincident(g347,g5)
    c: Coincident(g348,g5)
    c: Coincident(g348,g346)
    c: Coincident(g349,g6)
    c: Horizontal(g349)
    c: Coincident(g350,g6)
    c: Horizontal(g350)
